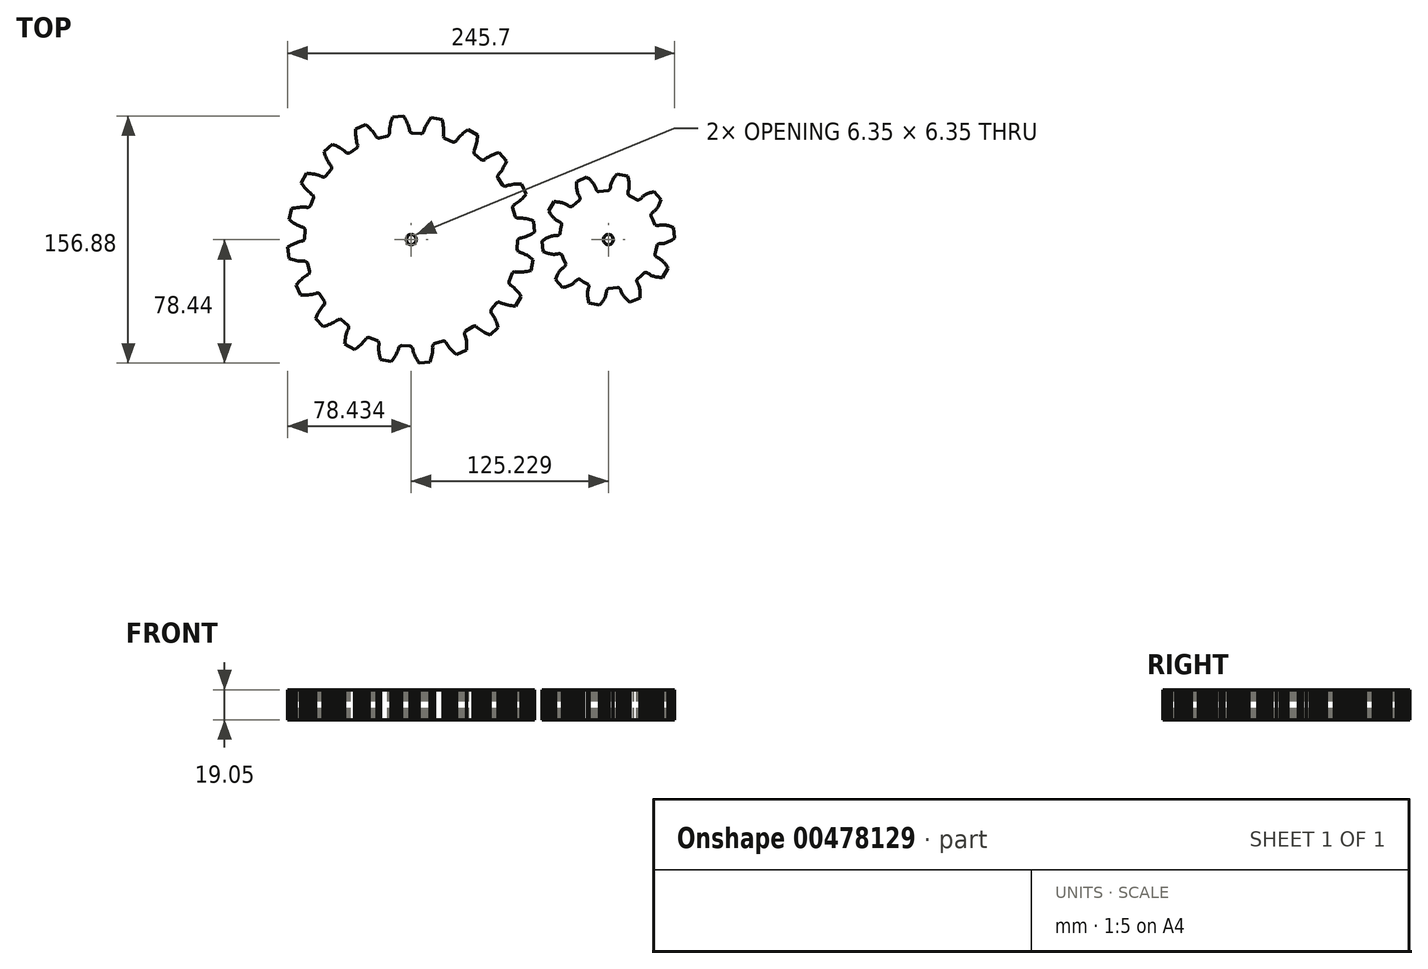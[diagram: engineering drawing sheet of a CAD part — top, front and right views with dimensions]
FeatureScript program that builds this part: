
annotation { "Feature Type Name" : "Feature", "Feature Type Description" : "" }
export const myFeature = defineFeature(function(context is Context, id is Id, definition is map)
    precondition{}
    {
        {
            var Q0;
            Q0=qCreatedBy(makeId("Top.planeOp"),FACE);
            var sketch = newSketch(context, id + "F0", { "sketchPlane" : qUnion([Q0])});
            skLineSegment(sketch, "E0", {"start": v(22.88, -6.1) * mm, "end": v(23.09, -6.86) * mm});
            skLineSegment(sketch, "E1", {"start": v(23.09, -6.86) * mm, "end": v(23.33, -7.16) * mm});
            skLineSegment(sketch, "E2", {"start": v(23.33, -7.16) * mm, "end": v(23.58, -7.39) * mm});
            skLineSegment(sketch, "E3", {"start": v(23.58, -7.39) * mm, "end": v(23.81, -7.8) * mm});
            skLineSegment(sketch, "E4", {"start": v(23.81, -7.8) * mm, "end": v(24.36, -7.91) * mm});
            skLineSegment(sketch, "E5", {"start": v(24.36, -7.91) * mm, "end": v(24.9, -8.06) * mm});
            skLineSegment(sketch, "E6", {"start": v(24.9, -8.06) * mm, "end": v(25.96, -8.43) * mm});
            skLineSegment(sketch, "E7", {"start": v(25.96, -8.43) * mm, "end": v(27.01, -8.88) * mm});
            skLineSegment(sketch, "E8", {"start": v(27.01, -8.88) * mm, "end": v(28.06, -9.39) * mm});
            skLineSegment(sketch, "E9", {"start": v(28.06, -9.39) * mm, "end": v(29.1, -9.95) * mm});
            skLineSegment(sketch, "E10", {"start": v(29.1, -9.95) * mm, "end": v(30.12, -10.57) * mm});
            skLineSegment(sketch, "E11", {"start": v(30.12, -10.57) * mm, "end": v(31.14, -11.24) * mm});
            skLineSegment(sketch, "E12", {"start": v(31.14, -11.24) * mm, "end": v(32.14, -11.96) * mm});
            skLineSegment(sketch, "E13", {"start": v(32.14, -11.96) * mm, "end": v(33.14, -12.72) * mm});
            skLineSegment(sketch, "E14", {"start": v(33.14, -12.72) * mm, "end": v(31.69, -19.6) * mm});
            skLineSegment(sketch, "E15", {"start": v(31.69, -19.6) * mm, "end": v(30.47, -19.9) * mm});
            skLineSegment(sketch, "E16", {"start": v(30.47, -19.9) * mm, "end": v(29.26, -20.15) * mm});
            skLineSegment(sketch, "E17", {"start": v(29.26, -20.15) * mm, "end": v(28.06, -20.35) * mm});
            skLineSegment(sketch, "E18", {"start": v(28.06, -20.35) * mm, "end": v(26.88, -20.5) * mm});
            skLineSegment(sketch, "E19", {"start": v(26.88, -20.5) * mm, "end": v(25.7, -20.6) * mm});
            skLineSegment(sketch, "E20", {"start": v(25.7, -20.6) * mm, "end": v(24.54, -20.65) * mm});
            skLineSegment(sketch, "E21", {"start": v(24.54, -20.65) * mm, "end": v(23.4, -20.64) * mm});
            skLineSegment(sketch, "E22", {"start": v(23.4, -20.64) * mm, "end": v(22.27, -20.55) * mm});
            skLineSegment(sketch, "E23", {"start": v(22.27, -20.55) * mm, "end": v(21.72, -20.47) * mm});
            skLineSegment(sketch, "E24", {"start": v(21.72, -20.47) * mm, "end": v(21.18, -20.35) * mm});
            skLineSegment(sketch, "E25", {"start": v(21.18, -20.35) * mm, "end": v(20.8, -20.64) * mm});
            skLineSegment(sketch, "E26", {"start": v(20.8, -20.64) * mm, "end": v(20.47, -20.74) * mm});
            skLineSegment(sketch, "E27", {"start": v(20.47, -20.74) * mm, "end": v(20.13, -20.92) * mm});
            skLineSegment(sketch, "E28", {"start": v(20.13, -20.92) * mm, "end": v(19.64, -21.53) * mm});
            skLineSegment(sketch, "E29", {"start": v(19.64, -21.53) * mm, "end": v(17.7, -26.6) * mm});
            skLineSegment(sketch, "E30", {"start": v(17.7, -26.6) * mm, "end": v(17.66, -27.38) * mm});
            skLineSegment(sketch, "E31", {"start": v(17.66, -27.38) * mm, "end": v(17.8, -27.74) * mm});
            skLineSegment(sketch, "E32", {"start": v(17.8, -27.74) * mm, "end": v(17.97, -28.04) * mm});
            skLineSegment(sketch, "E33", {"start": v(17.97, -28.04) * mm, "end": v(18.06, -28.5) * mm});
            skLineSegment(sketch, "E34", {"start": v(18.06, -28.5) * mm, "end": v(18.54, -28.78) * mm});
            skLineSegment(sketch, "E35", {"start": v(18.54, -28.78) * mm, "end": v(19, -29.09) * mm});
            skLineSegment(sketch, "E36", {"start": v(19, -29.09) * mm, "end": v(19.9, -29.77) * mm});
            skLineSegment(sketch, "E37", {"start": v(19.9, -29.77) * mm, "end": v(20.77, -30.52) * mm});
            skLineSegment(sketch, "E38", {"start": v(20.77, -30.52) * mm, "end": v(21.61, -31.32) * mm});
            skLineSegment(sketch, "E39", {"start": v(21.61, -31.32) * mm, "end": v(22.42, -32.18) * mm});
            skLineSegment(sketch, "E40", {"start": v(22.42, -32.18) * mm, "end": v(23.2, -33.09) * mm});
            skLineSegment(sketch, "E41", {"start": v(23.2, -33.09) * mm, "end": v(23.97, -34.04) * mm});
            skLineSegment(sketch, "E42", {"start": v(23.97, -34.04) * mm, "end": v(24.7, -35.03) * mm});
            skLineSegment(sketch, "E43", {"start": v(24.7, -35.03) * mm, "end": v(25.41, -36.06) * mm});
            skLineSegment(sketch, "E44", {"start": v(25.41, -36.06) * mm, "end": v(21.9, -42.16) * mm});
            skLineSegment(sketch, "E45", {"start": v(21.9, -42.16) * mm, "end": v(20.66, -42.07) * mm});
            skLineSegment(sketch, "E46", {"start": v(20.66, -42.07) * mm, "end": v(19.43, -41.93) * mm});
            skLineSegment(sketch, "E47", {"start": v(19.43, -41.93) * mm, "end": v(18.23, -41.76) * mm});
            skLineSegment(sketch, "E48", {"start": v(18.23, -41.76) * mm, "end": v(17.05, -41.53) * mm});
            skLineSegment(sketch, "E49", {"start": v(17.05, -41.53) * mm, "end": v(15.9, -41.27) * mm});
            skLineSegment(sketch, "E50", {"start": v(15.9, -41.27) * mm, "end": v(14.78, -40.95) * mm});
            skLineSegment(sketch, "E51", {"start": v(14.78, -40.95) * mm, "end": v(13.7, -40.58) * mm});
            skLineSegment(sketch, "E52", {"start": v(13.7, -40.58) * mm, "end": v(12.65, -40.15) * mm});
            skLineSegment(sketch, "E53", {"start": v(12.65, -40.15) * mm, "end": v(12.15, -39.9) * mm});
            skLineSegment(sketch, "E54", {"start": v(12.15, -39.9) * mm, "end": v(11.68, -39.62) * mm});
            skLineSegment(sketch, "E55", {"start": v(11.68, -39.62) * mm, "end": v(11.23, -39.78) * mm});
            skLineSegment(sketch, "E56", {"start": v(11.23, -39.78) * mm, "end": v(10.89, -39.78) * mm});
            skLineSegment(sketch, "E57", {"start": v(10.89, -39.78) * mm, "end": v(10.5, -39.84) * mm});
            skLineSegment(sketch, "E58", {"start": v(10.5, -39.84) * mm, "end": v(9.85, -40.27) * mm});
            skLineSegment(sketch, "E59", {"start": v(9.85, -40.27) * mm, "end": v(6.44, -44.5) * mm});
            skLineSegment(sketch, "E60", {"start": v(6.44, -44.5) * mm, "end": v(6.16, -45.22) * mm});
            skLineSegment(sketch, "E61", {"start": v(6.16, -45.22) * mm, "end": v(6.18, -45.61) * mm});
            skLineSegment(sketch, "E62", {"start": v(6.18, -45.61) * mm, "end": v(6.26, -45.94) * mm});
            skLineSegment(sketch, "E63", {"start": v(6.26, -45.94) * mm, "end": v(6.2, -46.42) * mm});
            skLineSegment(sketch, "E64", {"start": v(6.2, -46.42) * mm, "end": v(6.57, -46.83) * mm});
            skLineSegment(sketch, "E65", {"start": v(6.57, -46.83) * mm, "end": v(6.92, -47.26) * mm});
            skLineSegment(sketch, "E66", {"start": v(6.92, -47.26) * mm, "end": v(7.56, -48.19) * mm});
            skLineSegment(sketch, "E67", {"start": v(7.56, -48.19) * mm, "end": v(8.15, -49.17) * mm});
            skLineSegment(sketch, "E68", {"start": v(8.15, -49.17) * mm, "end": v(8.7, -50.2) * mm});
            skLineSegment(sketch, "E69", {"start": v(8.7, -50.2) * mm, "end": v(9.2, -51.26) * mm});
            skLineSegment(sketch, "E70", {"start": v(9.2, -51.26) * mm, "end": v(9.67, -52.37) * mm});
            skLineSegment(sketch, "E71", {"start": v(9.67, -52.37) * mm, "end": v(10.1, -53.5) * mm});
            skLineSegment(sketch, "E72", {"start": v(10.1, -53.5) * mm, "end": v(10.5, -54.68) * mm});
            skLineSegment(sketch, "E73", {"start": v(10.5, -54.68) * mm, "end": v(10.85, -55.87) * mm});
            skLineSegment(sketch, "E74", {"start": v(10.85, -55.87) * mm, "end": v(5.63, -60.6) * mm});
            skLineSegment(sketch, "E75", {"start": v(5.63, -60.6) * mm, "end": v(4.47, -60.12) * mm});
            skLineSegment(sketch, "E76", {"start": v(4.47, -60.12) * mm, "end": v(3.35, -59.61) * mm});
            skLineSegment(sketch, "E77", {"start": v(3.35, -59.61) * mm, "end": v(2.26, -59.07) * mm});
            skLineSegment(sketch, "E78", {"start": v(2.26, -59.07) * mm, "end": v(1.2, -58.5) * mm});
            skLineSegment(sketch, "E79", {"start": v(1.2, -58.5) * mm, "end": v(0.2, -57.89) * mm});
            skLineSegment(sketch, "E80", {"start": v(0.2, -57.89) * mm, "end": v(-0.77, -57.24) * mm});
            skLineSegment(sketch, "E81", {"start": v(-0.77, -57.24) * mm, "end": v(-1.69, -56.55) * mm});
            skLineSegment(sketch, "E82", {"start": v(-1.69, -56.55) * mm, "end": v(-2.54, -55.82) * mm});
            skLineSegment(sketch, "E83", {"start": v(-2.54, -55.82) * mm, "end": v(-2.94, -55.43) * mm});
            skLineSegment(sketch, "E84", {"start": v(-2.94, -55.43) * mm, "end": v(-3.31, -55.01) * mm});
            skLineSegment(sketch, "E85", {"start": v(-3.31, -55.01) * mm, "end": v(-3.79, -55.03) * mm});
            skLineSegment(sketch, "E86", {"start": v(-3.79, -55.03) * mm, "end": v(-4.11, -54.92) * mm});
            skLineSegment(sketch, "E87", {"start": v(-4.11, -54.92) * mm, "end": v(-4.5, -54.86) * mm});
            skLineSegment(sketch, "E88", {"start": v(-4.5, -54.86) * mm, "end": v(-5.25, -55.06) * mm});
            skLineSegment(sketch, "E89", {"start": v(-5.25, -55.06) * mm, "end": v(-9.8, -58.03) * mm});
            skLineSegment(sketch, "E90", {"start": v(-9.8, -58.03) * mm, "end": v(-10.29, -58.64) * mm});
            skLineSegment(sketch, "E91", {"start": v(-10.29, -58.64) * mm, "end": v(-10.39, -59.02) * mm});
            skLineSegment(sketch, "E92", {"start": v(-10.39, -59.02) * mm, "end": v(-10.42, -59.35) * mm});
            skLineSegment(sketch, "E93", {"start": v(-10.42, -59.35) * mm, "end": v(-10.63, -59.79) * mm});
            skLineSegment(sketch, "E94", {"start": v(-10.63, -59.79) * mm, "end": v(-10.4, -60.29) * mm});
            skLineSegment(sketch, "E95", {"start": v(-10.4, -60.29) * mm, "end": v(-10.2, -60.81) * mm});
            skLineSegment(sketch, "E96", {"start": v(-10.2, -60.81) * mm, "end": v(-9.87, -61.9) * mm});
            skLineSegment(sketch, "E97", {"start": v(-9.87, -61.9) * mm, "end": v(-9.61, -63) * mm});
            skLineSegment(sketch, "E98", {"start": v(-9.61, -63) * mm, "end": v(-9.4, -64.15) * mm});
            skLineSegment(sketch, "E99", {"start": v(-9.4, -64.15) * mm, "end": v(-9.26, -65.32) * mm});
            skLineSegment(sketch, "E100", {"start": v(-9.26, -65.32) * mm, "end": v(-9.16, -66.52) * mm});
            skLineSegment(sketch, "E101", {"start": v(-9.16, -66.52) * mm, "end": v(-9.1, -67.73) * mm});
            skLineSegment(sketch, "E102", {"start": v(-9.1, -67.73) * mm, "end": v(-9.09, -68.97) * mm});
            skLineSegment(sketch, "E103", {"start": v(-9.09, -68.97) * mm, "end": v(-9.12, -70.22) * mm});
            skLineSegment(sketch, "E104", {"start": v(-9.12, -70.22) * mm, "end": v(-15.54, -73.1) * mm});
            skLineSegment(sketch, "E105", {"start": v(-15.54, -73.1) * mm, "end": v(-16.5, -72.28) * mm});
            skLineSegment(sketch, "E106", {"start": v(-16.5, -72.28) * mm, "end": v(-17.41, -71.45) * mm});
            skLineSegment(sketch, "E107", {"start": v(-17.41, -71.45) * mm, "end": v(-18.28, -70.6) * mm});
            skLineSegment(sketch, "E108", {"start": v(-18.28, -70.6) * mm, "end": v(-19.1, -69.73) * mm});
            skLineSegment(sketch, "E109", {"start": v(-19.1, -69.73) * mm, "end": v(-19.88, -68.84) * mm});
            skLineSegment(sketch, "E110", {"start": v(-19.88, -68.84) * mm, "end": v(-20.6, -67.92) * mm});
            skLineSegment(sketch, "E111", {"start": v(-20.6, -67.92) * mm, "end": v(-21.26, -66.99) * mm});
            skLineSegment(sketch, "E112", {"start": v(-21.26, -66.99) * mm, "end": v(-21.84, -66.02) * mm});
            skLineSegment(sketch, "E113", {"start": v(-21.84, -66.02) * mm, "end": v(-22.1, -65.53) * mm});
            skLineSegment(sketch, "E114", {"start": v(-22.1, -65.53) * mm, "end": v(-22.32, -65.02) * mm});
            skLineSegment(sketch, "E115", {"start": v(-22.32, -65.02) * mm, "end": v(-22.78, -64.89) * mm});
            skLineSegment(sketch, "E116", {"start": v(-22.78, -64.89) * mm, "end": v(-23.06, -64.69) * mm});
            skLineSegment(sketch, "E117", {"start": v(-23.06, -64.69) * mm, "end": v(-23.4, -64.51) * mm});
            skLineSegment(sketch, "E118", {"start": v(-23.4, -64.51) * mm, "end": v(-24.18, -64.47) * mm});
            skLineSegment(sketch, "E119", {"start": v(-24.18, -64.47) * mm, "end": v(-29.43, -65.9) * mm});
            skLineSegment(sketch, "E120", {"start": v(-29.43, -65.9) * mm, "end": v(-30.08, -66.32) * mm});
            skLineSegment(sketch, "E121", {"start": v(-30.08, -66.32) * mm, "end": v(-30.3, -66.64) * mm});
            skLineSegment(sketch, "E122", {"start": v(-30.3, -66.64) * mm, "end": v(-30.43, -66.95) * mm});
            skLineSegment(sketch, "E123", {"start": v(-30.43, -66.95) * mm, "end": v(-30.75, -67.3) * mm});
            skLineSegment(sketch, "E124", {"start": v(-30.75, -67.3) * mm, "end": v(-30.7, -67.85) * mm});
            skLineSegment(sketch, "E125", {"start": v(-30.7, -67.85) * mm, "end": v(-30.67, -68.4) * mm});
            skLineSegment(sketch, "E126", {"start": v(-30.67, -68.4) * mm, "end": v(-30.69, -69.54) * mm});
            skLineSegment(sketch, "E127", {"start": v(-30.69, -69.54) * mm, "end": v(-30.79, -70.68) * mm});
            skLineSegment(sketch, "E128", {"start": v(-30.79, -70.68) * mm, "end": v(-30.95, -71.83) * mm});
            skLineSegment(sketch, "E129", {"start": v(-30.95, -71.83) * mm, "end": v(-31.17, -72.99) * mm});
            skLineSegment(sketch, "E130", {"start": v(-31.17, -72.99) * mm, "end": v(-31.44, -74.16) * mm});
            skLineSegment(sketch, "E131", {"start": v(-31.44, -74.16) * mm, "end": v(-31.76, -75.33) * mm});
            skLineSegment(sketch, "E132", {"start": v(-31.76, -75.33) * mm, "end": v(-32.13, -76.5) * mm});
            skLineSegment(sketch, "E133", {"start": v(-32.13, -76.5) * mm, "end": v(-32.55, -77.69) * mm});
            skLineSegment(sketch, "E134", {"start": v(-32.55, -77.69) * mm, "end": v(-39.54, -78.44) * mm});
            skLineSegment(sketch, "E135", {"start": v(-39.54, -78.44) * mm, "end": v(-40.2, -77.37) * mm});
            skLineSegment(sketch, "E136", {"start": v(-40.2, -77.37) * mm, "end": v(-40.81, -76.3) * mm});
            skLineSegment(sketch, "E137", {"start": v(-40.81, -76.3) * mm, "end": v(-41.38, -75.22) * mm});
            skLineSegment(sketch, "E138", {"start": v(-41.38, -75.22) * mm, "end": v(-41.89, -74.14) * mm});
            skLineSegment(sketch, "E139", {"start": v(-41.89, -74.14) * mm, "end": v(-42.35, -73.05) * mm});
            skLineSegment(sketch, "E140", {"start": v(-42.35, -73.05) * mm, "end": v(-42.75, -71.96) * mm});
            skLineSegment(sketch, "E141", {"start": v(-42.75, -71.96) * mm, "end": v(-43.09, -70.87) * mm});
            skLineSegment(sketch, "E142", {"start": v(-43.09, -70.87) * mm, "end": v(-43.35, -69.77) * mm});
            skLineSegment(sketch, "E143", {"start": v(-43.35, -69.77) * mm, "end": v(-43.44, -69.22) * mm});
            skLineSegment(sketch, "E144", {"start": v(-43.44, -69.22) * mm, "end": v(-43.5, -68.67) * mm});
            skLineSegment(sketch, "E145", {"start": v(-43.5, -68.67) * mm, "end": v(-43.9, -68.4) * mm});
            skLineSegment(sketch, "E146", {"start": v(-43.9, -68.4) * mm, "end": v(-44.1, -68.12) * mm});
            skLineSegment(sketch, "E147", {"start": v(-44.1, -68.12) * mm, "end": v(-44.37, -67.85) * mm});
            skLineSegment(sketch, "E148", {"start": v(-44.37, -67.85) * mm, "end": v(-45.1, -67.57) * mm});
            skLineSegment(sketch, "E149", {"start": v(-45.1, -67.57) * mm, "end": v(-50.52, -67.3) * mm});
            skLineSegment(sketch, "E150", {"start": v(-50.52, -67.3) * mm, "end": v(-51.27, -67.5) * mm});
            skLineSegment(sketch, "E151", {"start": v(-51.27, -67.5) * mm, "end": v(-51.58, -67.75) * mm});
            skLineSegment(sketch, "E152", {"start": v(-51.58, -67.75) * mm, "end": v(-51.8, -68) * mm});
            skLineSegment(sketch, "E153", {"start": v(-51.8, -68) * mm, "end": v(-52.22, -68.23) * mm});
            skLineSegment(sketch, "E154", {"start": v(-52.22, -68.23) * mm, "end": v(-52.33, -68.77) * mm});
            skLineSegment(sketch, "E155", {"start": v(-52.33, -68.77) * mm, "end": v(-52.48, -69.3) * mm});
            skLineSegment(sketch, "E156", {"start": v(-52.48, -69.3) * mm, "end": v(-52.85, -70.37) * mm});
            skLineSegment(sketch, "E157", {"start": v(-52.85, -70.37) * mm, "end": v(-53.3, -71.43) * mm});
            skLineSegment(sketch, "E158", {"start": v(-53.3, -71.43) * mm, "end": v(-53.8, -72.48) * mm});
            skLineSegment(sketch, "E159", {"start": v(-53.8, -72.48) * mm, "end": v(-54.37, -73.51) * mm});
            skLineSegment(sketch, "E160", {"start": v(-54.37, -73.51) * mm, "end": v(-54.99, -74.54) * mm});
            skLineSegment(sketch, "E161", {"start": v(-54.99, -74.54) * mm, "end": v(-55.66, -75.55) * mm});
            skLineSegment(sketch, "E162", {"start": v(-55.66, -75.55) * mm, "end": v(-56.37, -76.56) * mm});
            skLineSegment(sketch, "E163", {"start": v(-56.37, -76.56) * mm, "end": v(-57.14, -77.55) * mm});
            skLineSegment(sketch, "E164", {"start": v(-57.14, -77.55) * mm, "end": v(-64.02, -76.1) * mm});
            skLineSegment(sketch, "E165", {"start": v(-64.02, -76.1) * mm, "end": v(-64.32, -74.89) * mm});
            skLineSegment(sketch, "E166", {"start": v(-64.32, -74.89) * mm, "end": v(-64.57, -73.68) * mm});
            skLineSegment(sketch, "E167", {"start": v(-64.57, -73.68) * mm, "end": v(-64.77, -72.48) * mm});
            skLineSegment(sketch, "E168", {"start": v(-64.77, -72.48) * mm, "end": v(-64.92, -71.3) * mm});
            skLineSegment(sketch, "E169", {"start": v(-64.92, -71.3) * mm, "end": v(-65.03, -70.11) * mm});
            skLineSegment(sketch, "E170", {"start": v(-65.03, -70.11) * mm, "end": v(-65.07, -68.95) * mm});
            skLineSegment(sketch, "E171", {"start": v(-65.07, -68.95) * mm, "end": v(-65.05, -67.8) * mm});
            skLineSegment(sketch, "E172", {"start": v(-65.05, -67.8) * mm, "end": v(-64.96, -66.68) * mm});
            skLineSegment(sketch, "E173", {"start": v(-64.96, -66.68) * mm, "end": v(-64.88, -66.13) * mm});
            skLineSegment(sketch, "E174", {"start": v(-64.88, -66.13) * mm, "end": v(-64.76, -65.6) * mm});
            skLineSegment(sketch, "E175", {"start": v(-64.76, -65.6) * mm, "end": v(-65.05, -65.21) * mm});
            skLineSegment(sketch, "E176", {"start": v(-65.05, -65.21) * mm, "end": v(-65.16, -64.89) * mm});
            skLineSegment(sketch, "E177", {"start": v(-65.16, -64.89) * mm, "end": v(-65.34, -64.54) * mm});
            skLineSegment(sketch, "E178", {"start": v(-65.34, -64.54) * mm, "end": v(-65.94, -64.05) * mm});
            skLineSegment(sketch, "E179", {"start": v(-65.94, -64.05) * mm, "end": v(-71.02, -62.12) * mm});
            skLineSegment(sketch, "E180", {"start": v(-71.02, -62.12) * mm, "end": v(-71.8, -62.08) * mm});
            skLineSegment(sketch, "E181", {"start": v(-71.8, -62.08) * mm, "end": v(-72.16, -62.22) * mm});
            skLineSegment(sketch, "E182", {"start": v(-72.16, -62.22) * mm, "end": v(-72.45, -62.39) * mm});
            skLineSegment(sketch, "E183", {"start": v(-72.45, -62.39) * mm, "end": v(-72.92, -62.48) * mm});
            skLineSegment(sketch, "E184", {"start": v(-72.92, -62.48) * mm, "end": v(-73.2, -62.96) * mm});
            skLineSegment(sketch, "E185", {"start": v(-73.2, -62.96) * mm, "end": v(-73.5, -63.43) * mm});
            skLineSegment(sketch, "E186", {"start": v(-73.5, -63.43) * mm, "end": v(-74.18, -64.32) * mm});
            skLineSegment(sketch, "E187", {"start": v(-74.18, -64.32) * mm, "end": v(-74.93, -65.2) * mm});
            skLineSegment(sketch, "E188", {"start": v(-74.93, -65.2) * mm, "end": v(-75.74, -66.03) * mm});
            skLineSegment(sketch, "E189", {"start": v(-75.74, -66.03) * mm, "end": v(-76.6, -66.84) * mm});
            skLineSegment(sketch, "E190", {"start": v(-76.6, -66.84) * mm, "end": v(-77.5, -67.62) * mm});
            skLineSegment(sketch, "E191", {"start": v(-77.5, -67.62) * mm, "end": v(-78.46, -68.38) * mm});
            skLineSegment(sketch, "E192", {"start": v(-78.46, -68.38) * mm, "end": v(-79.45, -69.12) * mm});
            skLineSegment(sketch, "E193", {"start": v(-79.45, -69.12) * mm, "end": v(-80.48, -69.83) * mm});
            skLineSegment(sketch, "E194", {"start": v(-80.48, -69.83) * mm, "end": v(-86.58, -66.32) * mm});
            skLineSegment(sketch, "E195", {"start": v(-86.58, -66.32) * mm, "end": v(-86.48, -65.07) * mm});
            skLineSegment(sketch, "E196", {"start": v(-86.48, -65.07) * mm, "end": v(-86.35, -63.85) * mm});
            skLineSegment(sketch, "E197", {"start": v(-86.35, -63.85) * mm, "end": v(-86.17, -62.64) * mm});
            skLineSegment(sketch, "E198", {"start": v(-86.17, -62.64) * mm, "end": v(-85.95, -61.47) * mm});
            skLineSegment(sketch, "E199", {"start": v(-85.95, -61.47) * mm, "end": v(-85.68, -60.31) * mm});
            skLineSegment(sketch, "E200", {"start": v(-85.68, -60.31) * mm, "end": v(-85.37, -59.2) * mm});
            skLineSegment(sketch, "E201", {"start": v(-85.37, -59.2) * mm, "end": v(-85, -58.11) * mm});
            skLineSegment(sketch, "E202", {"start": v(-85, -58.11) * mm, "end": v(-84.56, -57.07) * mm});
            skLineSegment(sketch, "E203", {"start": v(-84.56, -57.07) * mm, "end": v(-84.31, -56.57) * mm});
            skLineSegment(sketch, "E204", {"start": v(-84.31, -56.57) * mm, "end": v(-84.04, -56.1) * mm});
            skLineSegment(sketch, "E205", {"start": v(-84.04, -56.1) * mm, "end": v(-84.2, -55.64) * mm});
            skLineSegment(sketch, "E206", {"start": v(-84.2, -55.64) * mm, "end": v(-84.2, -55.3) * mm});
            skLineSegment(sketch, "E207", {"start": v(-84.2, -55.3) * mm, "end": v(-84.26, -54.92) * mm});
            skLineSegment(sketch, "E208", {"start": v(-84.26, -54.92) * mm, "end": v(-84.68, -54.27) * mm});
            skLineSegment(sketch, "E209", {"start": v(-84.68, -54.27) * mm, "end": v(-88.91, -50.86) * mm});
            skLineSegment(sketch, "E210", {"start": v(-88.91, -50.86) * mm, "end": v(-89.64, -50.58) * mm});
            skLineSegment(sketch, "E211", {"start": v(-89.64, -50.58) * mm, "end": v(-90.03, -50.6) * mm});
            skLineSegment(sketch, "E212", {"start": v(-90.03, -50.6) * mm, "end": v(-90.36, -50.67) * mm});
            skLineSegment(sketch, "E213", {"start": v(-90.36, -50.67) * mm, "end": v(-90.83, -50.61) * mm});
            skLineSegment(sketch, "E214", {"start": v(-90.83, -50.61) * mm, "end": v(-91.24, -50.99) * mm});
            skLineSegment(sketch, "E215", {"start": v(-91.24, -50.99) * mm, "end": v(-91.68, -51.33) * mm});
            skLineSegment(sketch, "E216", {"start": v(-91.68, -51.33) * mm, "end": v(-92.6, -51.98) * mm});
            skLineSegment(sketch, "E217", {"start": v(-92.6, -51.98) * mm, "end": v(-93.58, -52.57) * mm});
            skLineSegment(sketch, "E218", {"start": v(-93.58, -52.57) * mm, "end": v(-94.61, -53.12) * mm});
            skLineSegment(sketch, "E219", {"start": v(-94.61, -53.12) * mm, "end": v(-95.68, -53.62) * mm});
            skLineSegment(sketch, "E220", {"start": v(-95.68, -53.62) * mm, "end": v(-96.78, -54.09) * mm});
            skLineSegment(sketch, "E221", {"start": v(-96.78, -54.09) * mm, "end": v(-97.92, -54.52) * mm});
            skLineSegment(sketch, "E222", {"start": v(-97.92, -54.52) * mm, "end": v(-99.1, -54.9) * mm});
            skLineSegment(sketch, "E223", {"start": v(-99.1, -54.9) * mm, "end": v(-100.3, -55.27) * mm});
            skLineSegment(sketch, "E224", {"start": v(-100.3, -55.27) * mm, "end": v(-105, -50.05) * mm});
            skLineSegment(sketch, "E225", {"start": v(-105, -50.05) * mm, "end": v(-104.53, -48.89) * mm});
            skLineSegment(sketch, "E226", {"start": v(-104.53, -48.89) * mm, "end": v(-104.03, -47.76) * mm});
            skLineSegment(sketch, "E227", {"start": v(-104.03, -47.76) * mm, "end": v(-103.49, -46.67) * mm});
            skLineSegment(sketch, "E228", {"start": v(-103.49, -46.67) * mm, "end": v(-102.91, -45.62) * mm});
            skLineSegment(sketch, "E229", {"start": v(-102.91, -45.62) * mm, "end": v(-102.3, -44.61) * mm});
            skLineSegment(sketch, "E230", {"start": v(-102.3, -44.61) * mm, "end": v(-101.65, -43.64) * mm});
            skLineSegment(sketch, "E231", {"start": v(-101.65, -43.64) * mm, "end": v(-100.97, -42.73) * mm});
            skLineSegment(sketch, "E232", {"start": v(-100.97, -42.73) * mm, "end": v(-100.23, -41.87) * mm});
            skLineSegment(sketch, "E233", {"start": v(-100.23, -41.87) * mm, "end": v(-99.84, -41.47) * mm});
            skLineSegment(sketch, "E234", {"start": v(-99.84, -41.47) * mm, "end": v(-99.43, -41.1) * mm});
            skLineSegment(sketch, "E235", {"start": v(-99.43, -41.1) * mm, "end": v(-99.44, -40.63) * mm});
            skLineSegment(sketch, "E236", {"start": v(-99.44, -40.63) * mm, "end": v(-99.34, -40.3) * mm});
            skLineSegment(sketch, "E237", {"start": v(-99.34, -40.3) * mm, "end": v(-99.28, -39.92) * mm});
            skLineSegment(sketch, "E238", {"start": v(-99.28, -39.92) * mm, "end": v(-99.48, -39.17) * mm});
            skLineSegment(sketch, "E239", {"start": v(-99.48, -39.17) * mm, "end": v(-102.45, -34.62) * mm});
            skLineSegment(sketch, "E240", {"start": v(-102.45, -34.62) * mm, "end": v(-103.06, -34.13) * mm});
            skLineSegment(sketch, "E241", {"start": v(-103.06, -34.13) * mm, "end": v(-103.43, -34.03) * mm});
            skLineSegment(sketch, "E242", {"start": v(-103.43, -34.03) * mm, "end": v(-103.77, -34) * mm});
            skLineSegment(sketch, "E243", {"start": v(-103.77, -34) * mm, "end": v(-104.2, -33.79) * mm});
            skLineSegment(sketch, "E244", {"start": v(-104.2, -33.79) * mm, "end": v(-104.7, -34.02) * mm});
            skLineSegment(sketch, "E245", {"start": v(-104.7, -34.02) * mm, "end": v(-105.23, -34.22) * mm});
            skLineSegment(sketch, "E246", {"start": v(-105.23, -34.22) * mm, "end": v(-106.3, -34.54) * mm});
            skLineSegment(sketch, "E247", {"start": v(-106.3, -34.54) * mm, "end": v(-107.42, -34.8) * mm});
            skLineSegment(sketch, "E248", {"start": v(-107.42, -34.8) * mm, "end": v(-108.57, -35) * mm});
            skLineSegment(sketch, "E249", {"start": v(-108.57, -35) * mm, "end": v(-109.74, -35.16) * mm});
            skLineSegment(sketch, "E250", {"start": v(-109.74, -35.16) * mm, "end": v(-110.93, -35.26) * mm});
            skLineSegment(sketch, "E251", {"start": v(-110.93, -35.26) * mm, "end": v(-112.15, -35.31) * mm});
            skLineSegment(sketch, "E252", {"start": v(-112.15, -35.31) * mm, "end": v(-113.38, -35.33) * mm});
            skLineSegment(sketch, "E253", {"start": v(-113.38, -35.33) * mm, "end": v(-114.63, -35.3) * mm});
            skLineSegment(sketch, "E254", {"start": v(-114.63, -35.3) * mm, "end": v(-117.5, -28.87) * mm});
            skLineSegment(sketch, "E255", {"start": v(-117.5, -28.87) * mm, "end": v(-116.7, -27.92) * mm});
            skLineSegment(sketch, "E256", {"start": v(-116.7, -27.92) * mm, "end": v(-115.87, -27) * mm});
            skLineSegment(sketch, "E257", {"start": v(-115.87, -27) * mm, "end": v(-115.02, -26.14) * mm});
            skLineSegment(sketch, "E258", {"start": v(-115.02, -26.14) * mm, "end": v(-114.15, -25.31) * mm});
            skLineSegment(sketch, "E259", {"start": v(-114.15, -25.31) * mm, "end": v(-113.25, -24.54) * mm});
            skLineSegment(sketch, "E260", {"start": v(-113.25, -24.54) * mm, "end": v(-112.34, -23.82) * mm});
            skLineSegment(sketch, "E261", {"start": v(-112.34, -23.82) * mm, "end": v(-111.4, -23.16) * mm});
            skLineSegment(sketch, "E262", {"start": v(-111.4, -23.16) * mm, "end": v(-110.44, -22.57) * mm});
            skLineSegment(sketch, "E263", {"start": v(-110.44, -22.57) * mm, "end": v(-109.95, -22.31) * mm});
            skLineSegment(sketch, "E264", {"start": v(-109.95, -22.31) * mm, "end": v(-109.44, -22.1) * mm});
            skLineSegment(sketch, "E265", {"start": v(-109.44, -22.1) * mm, "end": v(-109.3, -21.63) * mm});
            skLineSegment(sketch, "E266", {"start": v(-109.3, -21.63) * mm, "end": v(-109.1, -21.36) * mm});
            skLineSegment(sketch, "E267", {"start": v(-109.1, -21.36) * mm, "end": v(-108.93, -21.01) * mm});
            skLineSegment(sketch, "E268", {"start": v(-108.93, -21.01) * mm, "end": v(-108.89, -20.23) * mm});
            skLineSegment(sketch, "E269", {"start": v(-108.89, -20.23) * mm, "end": v(-110.3, -14.99) * mm});
            skLineSegment(sketch, "E270", {"start": v(-110.3, -14.99) * mm, "end": v(-110.73, -14.34) * mm});
            skLineSegment(sketch, "E271", {"start": v(-110.73, -14.34) * mm, "end": v(-111.06, -14.13) * mm});
            skLineSegment(sketch, "E272", {"start": v(-111.06, -14.13) * mm, "end": v(-111.37, -13.99) * mm});
            skLineSegment(sketch, "E273", {"start": v(-111.37, -13.99) * mm, "end": v(-111.72, -13.66) * mm});
            skLineSegment(sketch, "E274", {"start": v(-111.72, -13.66) * mm, "end": v(-112.27, -13.72) * mm});
            skLineSegment(sketch, "E275", {"start": v(-112.27, -13.72) * mm, "end": v(-112.82, -13.75) * mm});
            skLineSegment(sketch, "E276", {"start": v(-112.82, -13.75) * mm, "end": v(-113.95, -13.73) * mm});
            skLineSegment(sketch, "E277", {"start": v(-113.95, -13.73) * mm, "end": v(-115.1, -13.63) * mm});
            skLineSegment(sketch, "E278", {"start": v(-115.1, -13.63) * mm, "end": v(-116.25, -13.47) * mm});
            skLineSegment(sketch, "E279", {"start": v(-116.25, -13.47) * mm, "end": v(-117.4, -13.25) * mm});
            skLineSegment(sketch, "E280", {"start": v(-117.4, -13.25) * mm, "end": v(-118.57, -12.98) * mm});
            skLineSegment(sketch, "E281", {"start": v(-118.57, -12.98) * mm, "end": v(-119.75, -12.66) * mm});
            skLineSegment(sketch, "E282", {"start": v(-119.75, -12.66) * mm, "end": v(-120.92, -12.28) * mm});
            skLineSegment(sketch, "E283", {"start": v(-120.92, -12.28) * mm, "end": v(-122.1, -11.87) * mm});
            skLineSegment(sketch, "E284", {"start": v(-122.1, -11.87) * mm, "end": v(-122.85, -4.87) * mm});
            skLineSegment(sketch, "E285", {"start": v(-122.85, -4.87) * mm, "end": v(-121.79, -4.21) * mm});
            skLineSegment(sketch, "E286", {"start": v(-121.79, -4.21) * mm, "end": v(-120.72, -3.6) * mm});
            skLineSegment(sketch, "E287", {"start": v(-120.72, -3.6) * mm, "end": v(-119.64, -3.04) * mm});
            skLineSegment(sketch, "E288", {"start": v(-119.64, -3.04) * mm, "end": v(-118.56, -2.53) * mm});
            skLineSegment(sketch, "E289", {"start": v(-118.56, -2.53) * mm, "end": v(-117.47, -2.07) * mm});
            skLineSegment(sketch, "E290", {"start": v(-117.47, -2.07) * mm, "end": v(-116.38, -1.66) * mm});
            skLineSegment(sketch, "E291", {"start": v(-116.38, -1.66) * mm, "end": v(-115.28, -1.33) * mm});
            skLineSegment(sketch, "E292", {"start": v(-115.28, -1.33) * mm, "end": v(-114.18, -1.07) * mm});
            skLineSegment(sketch, "E293", {"start": v(-114.18, -1.07) * mm, "end": v(-113.63, -0.97) * mm});
            skLineSegment(sketch, "E294", {"start": v(-113.63, -0.97) * mm, "end": v(-113.08, -0.92) * mm});
            skLineSegment(sketch, "E295", {"start": v(-113.08, -0.92) * mm, "end": v(-112.81, -0.52) * mm});
            skLineSegment(sketch, "E296", {"start": v(-112.81, -0.52) * mm, "end": v(-112.54, -0.32) * mm});
            skLineSegment(sketch, "E297", {"start": v(-112.54, -0.32) * mm, "end": v(-112.26, -0.05) * mm});
            skLineSegment(sketch, "E298", {"start": v(-112.26, -0.05) * mm, "end": v(-111.99, 0.68) * mm});
            skLineSegment(sketch, "E299", {"start": v(-111.99, 0.68) * mm, "end": v(-111.71, 6.1) * mm});
            skLineSegment(sketch, "E300", {"start": v(-111.71, 6.1) * mm, "end": v(-111.92, 6.86) * mm});
            skLineSegment(sketch, "E301", {"start": v(-111.92, 6.86) * mm, "end": v(-112.16, 7.16) * mm});
            skLineSegment(sketch, "E302", {"start": v(-112.16, 7.16) * mm, "end": v(-112.42, 7.38) * mm});
            skLineSegment(sketch, "E303", {"start": v(-112.42, 7.38) * mm, "end": v(-112.65, 7.8) * mm});
            skLineSegment(sketch, "E304", {"start": v(-112.65, 7.8) * mm, "end": v(-113.19, 7.91) * mm});
            skLineSegment(sketch, "E305", {"start": v(-113.19, 7.91) * mm, "end": v(-113.72, 8.06) * mm});
            skLineSegment(sketch, "E306", {"start": v(-113.72, 8.06) * mm, "end": v(-114.8, 8.43) * mm});
            skLineSegment(sketch, "E307", {"start": v(-114.8, 8.43) * mm, "end": v(-115.85, 8.88) * mm});
            skLineSegment(sketch, "E308", {"start": v(-115.85, 8.88) * mm, "end": v(-116.9, 9.39) * mm});
            skLineSegment(sketch, "E309", {"start": v(-116.9, 9.39) * mm, "end": v(-117.93, 9.95) * mm});
            skLineSegment(sketch, "E310", {"start": v(-117.93, 9.95) * mm, "end": v(-118.95, 10.57) * mm});
            skLineSegment(sketch, "E311", {"start": v(-118.95, 10.57) * mm, "end": v(-119.97, 11.24) * mm});
            skLineSegment(sketch, "E312", {"start": v(-119.97, 11.24) * mm, "end": v(-120.97, 11.96) * mm});
            skLineSegment(sketch, "E313", {"start": v(-120.97, 11.96) * mm, "end": v(-121.97, 12.72) * mm});
            skLineSegment(sketch, "E314", {"start": v(-121.97, 12.72) * mm, "end": v(-120.52, 19.6) * mm});
            skLineSegment(sketch, "E315", {"start": v(-120.52, 19.6) * mm, "end": v(-119.3, 19.9) * mm});
            skLineSegment(sketch, "E316", {"start": v(-119.3, 19.9) * mm, "end": v(-118.1, 20.15) * mm});
            skLineSegment(sketch, "E317", {"start": v(-118.1, 20.15) * mm, "end": v(-116.9, 20.35) * mm});
            skLineSegment(sketch, "E318", {"start": v(-116.9, 20.35) * mm, "end": v(-115.7, 20.5) * mm});
            skLineSegment(sketch, "E319", {"start": v(-115.7, 20.5) * mm, "end": v(-114.53, 20.6) * mm});
            skLineSegment(sketch, "E320", {"start": v(-114.53, 20.6) * mm, "end": v(-113.37, 20.65) * mm});
            skLineSegment(sketch, "E321", {"start": v(-113.37, 20.65) * mm, "end": v(-112.22, 20.64) * mm});
            skLineSegment(sketch, "E322", {"start": v(-112.22, 20.64) * mm, "end": v(-111.1, 20.55) * mm});
            skLineSegment(sketch, "E323", {"start": v(-111.1, 20.55) * mm, "end": v(-110.55, 20.47) * mm});
            skLineSegment(sketch, "E324", {"start": v(-110.55, 20.47) * mm, "end": v(-110, 20.35) * mm});
            skLineSegment(sketch, "E325", {"start": v(-110, 20.35) * mm, "end": v(-109.63, 20.64) * mm});
            skLineSegment(sketch, "E326", {"start": v(-109.63, 20.64) * mm, "end": v(-109.3, 20.74) * mm});
            skLineSegment(sketch, "E327", {"start": v(-109.3, 20.74) * mm, "end": v(-108.96, 20.92) * mm});
            skLineSegment(sketch, "E328", {"start": v(-108.96, 20.92) * mm, "end": v(-108.47, 21.53) * mm});
            skLineSegment(sketch, "E329", {"start": v(-108.47, 21.53) * mm, "end": v(-106.53, 26.6) * mm});
            skLineSegment(sketch, "E330", {"start": v(-106.53, 26.6) * mm, "end": v(-106.5, 27.38) * mm});
            skLineSegment(sketch, "E331", {"start": v(-106.5, 27.38) * mm, "end": v(-106.63, 27.74) * mm});
            skLineSegment(sketch, "E332", {"start": v(-106.63, 27.74) * mm, "end": v(-106.8, 28.04) * mm});
            skLineSegment(sketch, "E333", {"start": v(-106.8, 28.04) * mm, "end": v(-106.9, 28.5) * mm});
            skLineSegment(sketch, "E334", {"start": v(-106.9, 28.5) * mm, "end": v(-107.38, 28.78) * mm});
            skLineSegment(sketch, "E335", {"start": v(-107.38, 28.78) * mm, "end": v(-107.84, 29.09) * mm});
            skLineSegment(sketch, "E336", {"start": v(-107.84, 29.09) * mm, "end": v(-108.74, 29.77) * mm});
            skLineSegment(sketch, "E337", {"start": v(-108.74, 29.77) * mm, "end": v(-109.6, 30.52) * mm});
            skLineSegment(sketch, "E338", {"start": v(-109.6, 30.52) * mm, "end": v(-110.44, 31.32) * mm});
            skLineSegment(sketch, "E339", {"start": v(-110.44, 31.32) * mm, "end": v(-111.25, 32.18) * mm});
            skLineSegment(sketch, "E340", {"start": v(-111.25, 32.18) * mm, "end": v(-112.04, 33.09) * mm});
            skLineSegment(sketch, "E341", {"start": v(-112.04, 33.09) * mm, "end": v(-112.8, 34.04) * mm});
            skLineSegment(sketch, "E342", {"start": v(-112.8, 34.04) * mm, "end": v(-113.53, 35.03) * mm});
            skLineSegment(sketch, "E343", {"start": v(-113.53, 35.03) * mm, "end": v(-114.24, 36.06) * mm});
            skLineSegment(sketch, "E344", {"start": v(-114.24, 36.06) * mm, "end": v(-110.74, 42.16) * mm});
            skLineSegment(sketch, "E345", {"start": v(-110.74, 42.16) * mm, "end": v(-109.49, 42.07) * mm});
            skLineSegment(sketch, "E346", {"start": v(-109.49, 42.07) * mm, "end": v(-108.26, 41.93) * mm});
            skLineSegment(sketch, "E347", {"start": v(-108.26, 41.93) * mm, "end": v(-107.06, 41.76) * mm});
            skLineSegment(sketch, "E348", {"start": v(-107.06, 41.76) * mm, "end": v(-105.88, 41.53) * mm});
            skLineSegment(sketch, "E349", {"start": v(-105.88, 41.53) * mm, "end": v(-104.73, 41.27) * mm});
            skLineSegment(sketch, "E350", {"start": v(-104.73, 41.27) * mm, "end": v(-103.61, 40.95) * mm});
            skLineSegment(sketch, "E351", {"start": v(-103.61, 40.95) * mm, "end": v(-102.53, 40.58) * mm});
            skLineSegment(sketch, "E352", {"start": v(-102.53, 40.58) * mm, "end": v(-101.49, 40.15) * mm});
            skLineSegment(sketch, "E353", {"start": v(-101.49, 40.15) * mm, "end": v(-100.99, 39.9) * mm});
            skLineSegment(sketch, "E354", {"start": v(-100.99, 39.9) * mm, "end": v(-100.5, 39.62) * mm});
            skLineSegment(sketch, "E355", {"start": v(-100.5, 39.62) * mm, "end": v(-100.06, 39.78) * mm});
            skLineSegment(sketch, "E356", {"start": v(-100.06, 39.78) * mm, "end": v(-99.72, 39.78) * mm});
            skLineSegment(sketch, "E357", {"start": v(-99.72, 39.78) * mm, "end": v(-99.33, 39.84) * mm});
            skLineSegment(sketch, "E358", {"start": v(-99.33, 39.84) * mm, "end": v(-98.68, 40.27) * mm});
            skLineSegment(sketch, "E359", {"start": v(-98.68, 40.27) * mm, "end": v(-95.27, 44.5) * mm});
            skLineSegment(sketch, "E360", {"start": v(-95.27, 44.5) * mm, "end": v(-95, 45.22) * mm});
            skLineSegment(sketch, "E361", {"start": v(-95, 45.22) * mm, "end": v(-95.02, 45.61) * mm});
            skLineSegment(sketch, "E362", {"start": v(-95.02, 45.61) * mm, "end": v(-95.09, 45.94) * mm});
            skLineSegment(sketch, "E363", {"start": v(-95.09, 45.94) * mm, "end": v(-95.03, 46.42) * mm});
            skLineSegment(sketch, "E364", {"start": v(-95.03, 46.42) * mm, "end": v(-95.4, 46.83) * mm});
            skLineSegment(sketch, "E365", {"start": v(-95.4, 46.83) * mm, "end": v(-95.75, 47.26) * mm});
            skLineSegment(sketch, "E366", {"start": v(-95.75, 47.26) * mm, "end": v(-96.4, 48.19) * mm});
            skLineSegment(sketch, "E367", {"start": v(-96.4, 48.19) * mm, "end": v(-96.99, 49.17) * mm});
            skLineSegment(sketch, "E368", {"start": v(-96.99, 49.17) * mm, "end": v(-97.53, 50.2) * mm});
            skLineSegment(sketch, "E369", {"start": v(-97.53, 50.2) * mm, "end": v(-98.04, 51.26) * mm});
            skLineSegment(sketch, "E370", {"start": v(-98.04, 51.26) * mm, "end": v(-98.5, 52.37) * mm});
            skLineSegment(sketch, "E371", {"start": v(-98.5, 52.37) * mm, "end": v(-98.93, 53.5) * mm});
            skLineSegment(sketch, "E372", {"start": v(-98.93, 53.5) * mm, "end": v(-99.32, 54.67) * mm});
            skLineSegment(sketch, "E373", {"start": v(-99.32, 54.67) * mm, "end": v(-99.68, 55.87) * mm});
            skLineSegment(sketch, "E374", {"start": v(-99.68, 55.87) * mm, "end": v(-94.46, 60.6) * mm});
            skLineSegment(sketch, "E375", {"start": v(-94.46, 60.6) * mm, "end": v(-93.3, 60.12) * mm});
            skLineSegment(sketch, "E376", {"start": v(-93.3, 60.12) * mm, "end": v(-92.18, 59.61) * mm});
            skLineSegment(sketch, "E377", {"start": v(-92.18, 59.61) * mm, "end": v(-91.09, 59.07) * mm});
            skLineSegment(sketch, "E378", {"start": v(-91.09, 59.07) * mm, "end": v(-90.04, 58.5) * mm});
            skLineSegment(sketch, "E379", {"start": v(-90.04, 58.5) * mm, "end": v(-89.03, 57.89) * mm});
            skLineSegment(sketch, "E380", {"start": v(-89.03, 57.89) * mm, "end": v(-88.06, 57.24) * mm});
            skLineSegment(sketch, "E381", {"start": v(-88.06, 57.24) * mm, "end": v(-87.14, 56.55) * mm});
            skLineSegment(sketch, "E382", {"start": v(-87.14, 56.55) * mm, "end": v(-86.29, 55.82) * mm});
            skLineSegment(sketch, "E383", {"start": v(-86.29, 55.82) * mm, "end": v(-85.89, 55.43) * mm});
            skLineSegment(sketch, "E384", {"start": v(-85.89, 55.43) * mm, "end": v(-85.52, 55.01) * mm});
            skLineSegment(sketch, "E385", {"start": v(-85.52, 55.01) * mm, "end": v(-85.04, 55.03) * mm});
            skLineSegment(sketch, "E386", {"start": v(-85.04, 55.03) * mm, "end": v(-84.72, 54.92) * mm});
            skLineSegment(sketch, "E387", {"start": v(-84.72, 54.92) * mm, "end": v(-84.33, 54.86) * mm});
            skLineSegment(sketch, "E388", {"start": v(-84.33, 54.86) * mm, "end": v(-83.58, 55.06) * mm});
            skLineSegment(sketch, "E389", {"start": v(-83.58, 55.06) * mm, "end": v(-79.03, 58.03) * mm});
            skLineSegment(sketch, "E390", {"start": v(-79.03, 58.03) * mm, "end": v(-78.55, 58.64) * mm});
            skLineSegment(sketch, "E391", {"start": v(-78.55, 58.64) * mm, "end": v(-78.44, 59.02) * mm});
            skLineSegment(sketch, "E392", {"start": v(-78.44, 59.02) * mm, "end": v(-78.41, 59.35) * mm});
            skLineSegment(sketch, "E393", {"start": v(-78.41, 59.35) * mm, "end": v(-78.2, 59.79) * mm});
            skLineSegment(sketch, "E394", {"start": v(-78.2, 59.79) * mm, "end": v(-78.44, 60.29) * mm});
            skLineSegment(sketch, "E395", {"start": v(-78.44, 60.29) * mm, "end": v(-78.63, 60.81) * mm});
            skLineSegment(sketch, "E396", {"start": v(-78.63, 60.81) * mm, "end": v(-78.96, 61.9) * mm});
            skLineSegment(sketch, "E397", {"start": v(-78.96, 61.9) * mm, "end": v(-79.22, 63) * mm});
            skLineSegment(sketch, "E398", {"start": v(-79.22, 63) * mm, "end": v(-79.42, 64.15) * mm});
            skLineSegment(sketch, "E399", {"start": v(-79.42, 64.15) * mm, "end": v(-79.57, 65.32) * mm});
            skLineSegment(sketch, "E400", {"start": v(-79.57, 65.32) * mm, "end": v(-79.67, 66.52) * mm});
            skLineSegment(sketch, "E401", {"start": v(-79.67, 66.52) * mm, "end": v(-79.73, 67.73) * mm});
            skLineSegment(sketch, "E402", {"start": v(-79.73, 67.73) * mm, "end": v(-79.74, 68.97) * mm});
            skLineSegment(sketch, "E403", {"start": v(-79.74, 68.97) * mm, "end": v(-79.71, 70.22) * mm});
            skLineSegment(sketch, "E404", {"start": v(-79.71, 70.22) * mm, "end": v(-73.29, 73.1) * mm});
            skLineSegment(sketch, "E405", {"start": v(-73.29, 73.1) * mm, "end": v(-72.33, 72.28) * mm});
            skLineSegment(sketch, "E406", {"start": v(-72.33, 72.28) * mm, "end": v(-71.42, 71.45) * mm});
            skLineSegment(sketch, "E407", {"start": v(-71.42, 71.45) * mm, "end": v(-70.55, 70.6) * mm});
            skLineSegment(sketch, "E408", {"start": v(-70.55, 70.6) * mm, "end": v(-69.73, 69.73) * mm});
            skLineSegment(sketch, "E409", {"start": v(-69.73, 69.73) * mm, "end": v(-68.95, 68.84) * mm});
            skLineSegment(sketch, "E410", {"start": v(-68.95, 68.84) * mm, "end": v(-68.24, 67.92) * mm});
            skLineSegment(sketch, "E411", {"start": v(-68.24, 67.92) * mm, "end": v(-67.58, 66.99) * mm});
            skLineSegment(sketch, "E412", {"start": v(-67.58, 66.99) * mm, "end": v(-66.99, 66.02) * mm});
            skLineSegment(sketch, "E413", {"start": v(-66.99, 66.02) * mm, "end": v(-66.73, 65.53) * mm});
            skLineSegment(sketch, "E414", {"start": v(-66.73, 65.53) * mm, "end": v(-66.5, 65.02) * mm});
            skLineSegment(sketch, "E415", {"start": v(-66.5, 65.02) * mm, "end": v(-66.05, 64.89) * mm});
            skLineSegment(sketch, "E416", {"start": v(-66.05, 64.89) * mm, "end": v(-65.78, 64.69) * mm});
            skLineSegment(sketch, "E417", {"start": v(-65.78, 64.69) * mm, "end": v(-65.43, 64.51) * mm});
            skLineSegment(sketch, "E418", {"start": v(-65.43, 64.51) * mm, "end": v(-64.65, 64.47) * mm});
            skLineSegment(sketch, "E419", {"start": v(-64.65, 64.47) * mm, "end": v(-59.4, 65.9) * mm});
            skLineSegment(sketch, "E420", {"start": v(-59.4, 65.9) * mm, "end": v(-58.75, 66.32) * mm});
            skLineSegment(sketch, "E421", {"start": v(-58.75, 66.32) * mm, "end": v(-58.54, 66.64) * mm});
            skLineSegment(sketch, "E422", {"start": v(-58.54, 66.64) * mm, "end": v(-58.4, 66.95) * mm});
            skLineSegment(sketch, "E423", {"start": v(-58.4, 66.95) * mm, "end": v(-58.08, 67.3) * mm});
            skLineSegment(sketch, "E424", {"start": v(-58.08, 67.3) * mm, "end": v(-58.14, 67.85) * mm});
            skLineSegment(sketch, "E425", {"start": v(-58.14, 67.85) * mm, "end": v(-58.17, 68.4) * mm});
            skLineSegment(sketch, "E426", {"start": v(-58.17, 68.4) * mm, "end": v(-58.14, 69.54) * mm});
            skLineSegment(sketch, "E427", {"start": v(-58.14, 69.54) * mm, "end": v(-58.05, 70.68) * mm});
            skLineSegment(sketch, "E428", {"start": v(-58.05, 70.68) * mm, "end": v(-57.88, 71.83) * mm});
            skLineSegment(sketch, "E429", {"start": v(-57.88, 71.83) * mm, "end": v(-57.67, 72.99) * mm});
            skLineSegment(sketch, "E430", {"start": v(-57.67, 72.99) * mm, "end": v(-57.4, 74.16) * mm});
            skLineSegment(sketch, "E431", {"start": v(-57.4, 74.16) * mm, "end": v(-57.07, 75.33) * mm});
            skLineSegment(sketch, "E432", {"start": v(-57.07, 75.33) * mm, "end": v(-56.7, 76.5) * mm});
            skLineSegment(sketch, "E433", {"start": v(-56.7, 76.5) * mm, "end": v(-56.28, 77.69) * mm});
            skLineSegment(sketch, "E434", {"start": v(-56.28, 77.69) * mm, "end": v(-49.29, 78.44) * mm});
            skLineSegment(sketch, "E435", {"start": v(-49.29, 78.44) * mm, "end": v(-48.63, 77.37) * mm});
            skLineSegment(sketch, "E436", {"start": v(-48.63, 77.37) * mm, "end": v(-48.02, 76.3) * mm});
            skLineSegment(sketch, "E437", {"start": v(-48.02, 76.3) * mm, "end": v(-47.46, 75.22) * mm});
            skLineSegment(sketch, "E438", {"start": v(-47.46, 75.22) * mm, "end": v(-46.94, 74.14) * mm});
            skLineSegment(sketch, "E439", {"start": v(-46.94, 74.14) * mm, "end": v(-46.48, 73.05) * mm});
            skLineSegment(sketch, "E440", {"start": v(-46.48, 73.05) * mm, "end": v(-46.08, 71.96) * mm});
            skLineSegment(sketch, "E441", {"start": v(-46.08, 71.96) * mm, "end": v(-45.74, 70.87) * mm});
            skLineSegment(sketch, "E442", {"start": v(-45.74, 70.87) * mm, "end": v(-45.48, 69.77) * mm});
            skLineSegment(sketch, "E443", {"start": v(-45.48, 69.77) * mm, "end": v(-45.39, 69.22) * mm});
            skLineSegment(sketch, "E444", {"start": v(-45.39, 69.22) * mm, "end": v(-45.33, 68.67) * mm});
            skLineSegment(sketch, "E445", {"start": v(-45.33, 68.67) * mm, "end": v(-44.94, 68.4) * mm});
            skLineSegment(sketch, "E446", {"start": v(-44.94, 68.4) * mm, "end": v(-44.74, 68.12) * mm});
            skLineSegment(sketch, "E447", {"start": v(-44.74, 68.12) * mm, "end": v(-44.46, 67.85) * mm});
            skLineSegment(sketch, "E448", {"start": v(-44.46, 67.85) * mm, "end": v(-43.74, 67.57) * mm});
            skLineSegment(sketch, "E449", {"start": v(-43.74, 67.57) * mm, "end": v(-38.3, 67.3) * mm});
            skLineSegment(sketch, "E450", {"start": v(-38.3, 67.3) * mm, "end": v(-37.56, 67.5) * mm});
            skLineSegment(sketch, "E451", {"start": v(-37.56, 67.5) * mm, "end": v(-37.26, 67.75) * mm});
            skLineSegment(sketch, "E452", {"start": v(-37.26, 67.75) * mm, "end": v(-37.03, 68) * mm});
            skLineSegment(sketch, "E453", {"start": v(-37.03, 68) * mm, "end": v(-36.61, 68.23) * mm});
            skLineSegment(sketch, "E454", {"start": v(-36.61, 68.23) * mm, "end": v(-36.5, 68.77) * mm});
            skLineSegment(sketch, "E455", {"start": v(-36.5, 68.77) * mm, "end": v(-36.35, 69.3) * mm});
            skLineSegment(sketch, "E456", {"start": v(-36.35, 69.3) * mm, "end": v(-35.98, 70.37) * mm});
            skLineSegment(sketch, "E457", {"start": v(-35.98, 70.37) * mm, "end": v(-35.54, 71.43) * mm});
            skLineSegment(sketch, "E458", {"start": v(-35.54, 71.43) * mm, "end": v(-35.03, 72.48) * mm});
            skLineSegment(sketch, "E459", {"start": v(-35.03, 72.48) * mm, "end": v(-34.46, 73.51) * mm});
            skLineSegment(sketch, "E460", {"start": v(-34.46, 73.51) * mm, "end": v(-33.84, 74.54) * mm});
            skLineSegment(sketch, "E461", {"start": v(-33.84, 74.54) * mm, "end": v(-33.17, 75.55) * mm});
            skLineSegment(sketch, "E462", {"start": v(-33.17, 75.55) * mm, "end": v(-32.46, 76.56) * mm});
            skLineSegment(sketch, "E463", {"start": v(-32.46, 76.56) * mm, "end": v(-31.7, 77.55) * mm});
            skLineSegment(sketch, "E464", {"start": v(-31.7, 77.55) * mm, "end": v(-24.81, 76.1) * mm});
            skLineSegment(sketch, "E465", {"start": v(-24.81, 76.1) * mm, "end": v(-24.51, 74.89) * mm});
            skLineSegment(sketch, "E466", {"start": v(-24.51, 74.89) * mm, "end": v(-24.26, 73.68) * mm});
            skLineSegment(sketch, "E467", {"start": v(-24.26, 73.68) * mm, "end": v(-24.06, 72.48) * mm});
            skLineSegment(sketch, "E468", {"start": v(-24.06, 72.48) * mm, "end": v(-23.9, 71.3) * mm});
            skLineSegment(sketch, "E469", {"start": v(-23.9, 71.3) * mm, "end": v(-23.8, 70.11) * mm});
            skLineSegment(sketch, "E470", {"start": v(-23.8, 70.11) * mm, "end": v(-23.76, 68.95) * mm});
            skLineSegment(sketch, "E471", {"start": v(-23.76, 68.95) * mm, "end": v(-23.78, 67.8) * mm});
            skLineSegment(sketch, "E472", {"start": v(-23.78, 67.8) * mm, "end": v(-23.87, 66.68) * mm});
            skLineSegment(sketch, "E473", {"start": v(-23.87, 66.68) * mm, "end": v(-23.95, 66.13) * mm});
            skLineSegment(sketch, "E474", {"start": v(-23.95, 66.13) * mm, "end": v(-24.07, 65.6) * mm});
            skLineSegment(sketch, "E475", {"start": v(-24.07, 65.6) * mm, "end": v(-23.78, 65.21) * mm});
            skLineSegment(sketch, "E476", {"start": v(-23.78, 65.21) * mm, "end": v(-23.67, 64.89) * mm});
            skLineSegment(sketch, "E477", {"start": v(-23.67, 64.89) * mm, "end": v(-23.5, 64.54) * mm});
            skLineSegment(sketch, "E478", {"start": v(-23.5, 64.54) * mm, "end": v(-22.9, 64.05) * mm});
            skLineSegment(sketch, "E479", {"start": v(-22.9, 64.05) * mm, "end": v(-17.81, 62.12) * mm});
            skLineSegment(sketch, "E480", {"start": v(-17.81, 62.12) * mm, "end": v(-17.04, 62.08) * mm});
            skLineSegment(sketch, "E481", {"start": v(-17.04, 62.08) * mm, "end": v(-16.67, 62.22) * mm});
            skLineSegment(sketch, "E482", {"start": v(-16.67, 62.22) * mm, "end": v(-16.38, 62.39) * mm});
            skLineSegment(sketch, "E483", {"start": v(-16.38, 62.39) * mm, "end": v(-15.9, 62.48) * mm});
            skLineSegment(sketch, "E484", {"start": v(-15.9, 62.48) * mm, "end": v(-15.64, 62.96) * mm});
            skLineSegment(sketch, "E485", {"start": v(-15.64, 62.96) * mm, "end": v(-15.33, 63.43) * mm});
            skLineSegment(sketch, "E486", {"start": v(-15.33, 63.43) * mm, "end": v(-14.65, 64.32) * mm});
            skLineSegment(sketch, "E487", {"start": v(-14.65, 64.32) * mm, "end": v(-13.9, 65.2) * mm});
            skLineSegment(sketch, "E488", {"start": v(-13.9, 65.2) * mm, "end": v(-13.1, 66.03) * mm});
            skLineSegment(sketch, "E489", {"start": v(-13.1, 66.03) * mm, "end": v(-12.23, 66.84) * mm});
            skLineSegment(sketch, "E490", {"start": v(-12.23, 66.84) * mm, "end": v(-11.33, 67.62) * mm});
            skLineSegment(sketch, "E491", {"start": v(-11.33, 67.62) * mm, "end": v(-10.38, 68.38) * mm});
            skLineSegment(sketch, "E492", {"start": v(-10.38, 68.38) * mm, "end": v(-9.38, 69.12) * mm});
            skLineSegment(sketch, "E493", {"start": v(-9.38, 69.12) * mm, "end": v(-8.35, 69.83) * mm});
            skLineSegment(sketch, "E494", {"start": v(-8.35, 69.83) * mm, "end": v(-2.25, 66.32) * mm});
            skLineSegment(sketch, "E495", {"start": v(-2.25, 66.32) * mm, "end": v(-2.35, 65.07) * mm});
            skLineSegment(sketch, "E496", {"start": v(-2.35, 65.07) * mm, "end": v(-2.48, 63.85) * mm});
            skLineSegment(sketch, "E497", {"start": v(-2.48, 63.85) * mm, "end": v(-2.66, 62.64) * mm});
            skLineSegment(sketch, "E498", {"start": v(-2.66, 62.64) * mm, "end": v(-2.88, 61.46) * mm});
            skLineSegment(sketch, "E499", {"start": v(-2.88, 61.46) * mm, "end": v(-3.15, 60.31) * mm});
            skLineSegment(sketch, "E500", {"start": v(-3.15, 60.31) * mm, "end": v(-3.46, 59.2) * mm});
            skLineSegment(sketch, "E501", {"start": v(-3.46, 59.2) * mm, "end": v(-3.84, 58.11) * mm});
            skLineSegment(sketch, "E502", {"start": v(-3.84, 58.11) * mm, "end": v(-4.27, 57.07) * mm});
            skLineSegment(sketch, "E503", {"start": v(-4.27, 57.07) * mm, "end": v(-4.52, 56.57) * mm});
            skLineSegment(sketch, "E504", {"start": v(-4.52, 56.57) * mm, "end": v(-4.8, 56.1) * mm});
            skLineSegment(sketch, "E505", {"start": v(-4.8, 56.1) * mm, "end": v(-4.64, 55.64) * mm});
            skLineSegment(sketch, "E506", {"start": v(-4.64, 55.64) * mm, "end": v(-4.64, 55.3) * mm});
            skLineSegment(sketch, "E507", {"start": v(-4.64, 55.3) * mm, "end": v(-4.57, 54.92) * mm});
            skLineSegment(sketch, "E508", {"start": v(-4.57, 54.92) * mm, "end": v(-4.15, 54.27) * mm});
            skLineSegment(sketch, "E509", {"start": v(-4.15, 54.27) * mm, "end": v(0.08, 50.86) * mm});
            skLineSegment(sketch, "E510", {"start": v(0.08, 50.86) * mm, "end": v(0.8, 50.58) * mm});
            skLineSegment(sketch, "E511", {"start": v(0.8, 50.58) * mm, "end": v(1.2, 50.6) * mm});
            skLineSegment(sketch, "E512", {"start": v(1.2, 50.6) * mm, "end": v(1.53, 50.67) * mm});
            skLineSegment(sketch, "E513", {"start": v(1.53, 50.67) * mm, "end": v(2, 50.61) * mm});
            skLineSegment(sketch, "E514", {"start": v(2, 50.61) * mm, "end": v(2.41, 50.99) * mm});
            skLineSegment(sketch, "E515", {"start": v(2.41, 50.99) * mm, "end": v(2.85, 51.33) * mm});
            skLineSegment(sketch, "E516", {"start": v(2.85, 51.33) * mm, "end": v(3.77, 51.98) * mm});
            skLineSegment(sketch, "E517", {"start": v(3.77, 51.98) * mm, "end": v(4.75, 52.57) * mm});
            skLineSegment(sketch, "E518", {"start": v(4.75, 52.57) * mm, "end": v(5.78, 53.12) * mm});
            skLineSegment(sketch, "E519", {"start": v(5.78, 53.12) * mm, "end": v(6.85, 53.62) * mm});
            skLineSegment(sketch, "E520", {"start": v(6.85, 53.62) * mm, "end": v(7.95, 54.09) * mm});
            skLineSegment(sketch, "E521", {"start": v(7.95, 54.09) * mm, "end": v(9.09, 54.52) * mm});
            skLineSegment(sketch, "E522", {"start": v(9.09, 54.52) * mm, "end": v(10.26, 54.9) * mm});
            skLineSegment(sketch, "E523", {"start": v(10.26, 54.9) * mm, "end": v(11.46, 55.27) * mm});
            skLineSegment(sketch, "E524", {"start": v(11.46, 55.27) * mm, "end": v(16.18, 50.05) * mm});
            skLineSegment(sketch, "E525", {"start": v(16.18, 50.05) * mm, "end": v(15.7, 48.89) * mm});
            skLineSegment(sketch, "E526", {"start": v(15.7, 48.89) * mm, "end": v(15.2, 47.76) * mm});
            skLineSegment(sketch, "E527", {"start": v(15.2, 47.76) * mm, "end": v(14.65, 46.67) * mm});
            skLineSegment(sketch, "E528", {"start": v(14.65, 46.67) * mm, "end": v(14.08, 45.62) * mm});
            skLineSegment(sketch, "E529", {"start": v(14.08, 45.62) * mm, "end": v(13.47, 44.61) * mm});
            skLineSegment(sketch, "E530", {"start": v(13.47, 44.61) * mm, "end": v(12.82, 43.64) * mm});
            skLineSegment(sketch, "E531", {"start": v(12.82, 43.64) * mm, "end": v(12.14, 42.73) * mm});
            skLineSegment(sketch, "E532", {"start": v(12.14, 42.73) * mm, "end": v(11.4, 41.87) * mm});
            skLineSegment(sketch, "E533", {"start": v(11.4, 41.87) * mm, "end": v(11.01, 41.47) * mm});
            skLineSegment(sketch, "E534", {"start": v(11.01, 41.47) * mm, "end": v(10.6, 41.1) * mm});
            skLineSegment(sketch, "E535", {"start": v(10.6, 41.1) * mm, "end": v(10.61, 40.63) * mm});
            skLineSegment(sketch, "E536", {"start": v(10.61, 40.63) * mm, "end": v(10.5, 40.3) * mm});
            skLineSegment(sketch, "E537", {"start": v(10.5, 40.3) * mm, "end": v(10.45, 39.92) * mm});
            skLineSegment(sketch, "E538", {"start": v(10.45, 39.92) * mm, "end": v(10.65, 39.17) * mm});
            skLineSegment(sketch, "E539", {"start": v(10.65, 39.17) * mm, "end": v(13.62, 34.62) * mm});
            skLineSegment(sketch, "E540", {"start": v(13.62, 34.62) * mm, "end": v(14.22, 34.13) * mm});
            skLineSegment(sketch, "E541", {"start": v(14.22, 34.13) * mm, "end": v(14.6, 34.03) * mm});
            skLineSegment(sketch, "E542", {"start": v(14.6, 34.03) * mm, "end": v(14.94, 34) * mm});
            skLineSegment(sketch, "E543", {"start": v(14.94, 34) * mm, "end": v(15.37, 33.79) * mm});
            skLineSegment(sketch, "E544", {"start": v(15.37, 33.79) * mm, "end": v(15.87, 34.02) * mm});
            skLineSegment(sketch, "E545", {"start": v(15.87, 34.02) * mm, "end": v(16.4, 34.22) * mm});
            skLineSegment(sketch, "E546", {"start": v(16.4, 34.22) * mm, "end": v(17.47, 34.54) * mm});
            skLineSegment(sketch, "E547", {"start": v(17.47, 34.54) * mm, "end": v(18.6, 34.8) * mm});
            skLineSegment(sketch, "E548", {"start": v(18.6, 34.8) * mm, "end": v(19.74, 35) * mm});
            skLineSegment(sketch, "E549", {"start": v(19.74, 35) * mm, "end": v(20.9, 35.16) * mm});
            skLineSegment(sketch, "E550", {"start": v(20.9, 35.16) * mm, "end": v(22.1, 35.26) * mm});
            skLineSegment(sketch, "E551", {"start": v(22.1, 35.26) * mm, "end": v(23.32, 35.31) * mm});
            skLineSegment(sketch, "E552", {"start": v(23.32, 35.31) * mm, "end": v(24.55, 35.33) * mm});
            skLineSegment(sketch, "E553", {"start": v(24.55, 35.33) * mm, "end": v(25.8, 35.3) * mm});
            skLineSegment(sketch, "E554", {"start": v(25.8, 35.3) * mm, "end": v(28.68, 28.87) * mm});
            skLineSegment(sketch, "E555", {"start": v(28.68, 28.87) * mm, "end": v(27.87, 27.92) * mm});
            skLineSegment(sketch, "E556", {"start": v(27.87, 27.92) * mm, "end": v(27.04, 27) * mm});
            skLineSegment(sketch, "E557", {"start": v(27.04, 27) * mm, "end": v(26.19, 26.14) * mm});
            skLineSegment(sketch, "E558", {"start": v(26.19, 26.14) * mm, "end": v(25.31, 25.31) * mm});
            skLineSegment(sketch, "E559", {"start": v(25.31, 25.31) * mm, "end": v(24.42, 24.54) * mm});
            skLineSegment(sketch, "E560", {"start": v(24.42, 24.54) * mm, "end": v(23.5, 23.82) * mm});
            skLineSegment(sketch, "E561", {"start": v(23.5, 23.82) * mm, "end": v(22.57, 23.16) * mm});
            skLineSegment(sketch, "E562", {"start": v(22.57, 23.16) * mm, "end": v(21.6, 22.57) * mm});
            skLineSegment(sketch, "E563", {"start": v(21.6, 22.57) * mm, "end": v(21.11, 22.31) * mm});
            skLineSegment(sketch, "E564", {"start": v(21.11, 22.31) * mm, "end": v(20.6, 22.1) * mm});
            skLineSegment(sketch, "E565", {"start": v(20.6, 22.1) * mm, "end": v(20.47, 21.63) * mm});
            skLineSegment(sketch, "E566", {"start": v(20.47, 21.63) * mm, "end": v(20.27, 21.36) * mm});
            skLineSegment(sketch, "E567", {"start": v(20.27, 21.36) * mm, "end": v(20.1, 21.01) * mm});
            skLineSegment(sketch, "E568", {"start": v(20.1, 21.01) * mm, "end": v(20.06, 20.23) * mm});
            skLineSegment(sketch, "E569", {"start": v(20.06, 20.23) * mm, "end": v(21.47, 14.99) * mm});
            skLineSegment(sketch, "E570", {"start": v(21.47, 14.99) * mm, "end": v(21.9, 14.34) * mm});
            skLineSegment(sketch, "E571", {"start": v(21.9, 14.34) * mm, "end": v(22.23, 14.13) * mm});
            skLineSegment(sketch, "E572", {"start": v(22.23, 14.13) * mm, "end": v(22.54, 13.99) * mm});
            skLineSegment(sketch, "E573", {"start": v(22.54, 13.99) * mm, "end": v(22.89, 13.66) * mm});
            skLineSegment(sketch, "E574", {"start": v(22.89, 13.66) * mm, "end": v(23.44, 13.72) * mm});
            skLineSegment(sketch, "E575", {"start": v(23.44, 13.72) * mm, "end": v(24, 13.75) * mm});
            skLineSegment(sketch, "E576", {"start": v(24, 13.75) * mm, "end": v(25.12, 13.73) * mm});
            skLineSegment(sketch, "E577", {"start": v(25.12, 13.73) * mm, "end": v(26.26, 13.63) * mm});
            skLineSegment(sketch, "E578", {"start": v(26.26, 13.63) * mm, "end": v(27.41, 13.47) * mm});
            skLineSegment(sketch, "E579", {"start": v(27.41, 13.47) * mm, "end": v(28.57, 13.25) * mm});
            skLineSegment(sketch, "E580", {"start": v(28.57, 13.25) * mm, "end": v(29.74, 12.98) * mm});
            skLineSegment(sketch, "E581", {"start": v(29.74, 12.98) * mm, "end": v(30.91, 12.66) * mm});
            skLineSegment(sketch, "E582", {"start": v(30.91, 12.66) * mm, "end": v(32.1, 12.28) * mm});
            skLineSegment(sketch, "E583", {"start": v(32.1, 12.28) * mm, "end": v(33.27, 11.87) * mm});
            skLineSegment(sketch, "E584", {"start": v(33.27, 11.87) * mm, "end": v(34.02, 4.87) * mm});
            skLineSegment(sketch, "E585", {"start": v(34.02, 4.87) * mm, "end": v(32.96, 4.21) * mm});
            skLineSegment(sketch, "E586", {"start": v(32.96, 4.21) * mm, "end": v(31.89, 3.6) * mm});
            skLineSegment(sketch, "E587", {"start": v(31.89, 3.6) * mm, "end": v(30.8, 3.04) * mm});
            skLineSegment(sketch, "E588", {"start": v(30.8, 3.04) * mm, "end": v(29.72, 2.53) * mm});
            skLineSegment(sketch, "E589", {"start": v(29.72, 2.53) * mm, "end": v(28.64, 2.07) * mm});
            skLineSegment(sketch, "E590", {"start": v(28.64, 2.07) * mm, "end": v(27.54, 1.66) * mm});
            skLineSegment(sketch, "E591", {"start": v(27.54, 1.66) * mm, "end": v(26.45, 1.33) * mm});
            skLineSegment(sketch, "E592", {"start": v(26.45, 1.33) * mm, "end": v(25.35, 1.07) * mm});
            skLineSegment(sketch, "E593", {"start": v(25.35, 1.07) * mm, "end": v(24.8, 0.97) * mm});
            skLineSegment(sketch, "E594", {"start": v(24.8, 0.97) * mm, "end": v(24.25, 0.92) * mm});
            skLineSegment(sketch, "E595", {"start": v(24.25, 0.92) * mm, "end": v(23.98, 0.52) * mm});
            skLineSegment(sketch, "E596", {"start": v(23.98, 0.52) * mm, "end": v(23.7, 0.32) * mm});
            skLineSegment(sketch, "E597", {"start": v(23.7, 0.32) * mm, "end": v(23.43, 0.05) * mm});
            skLineSegment(sketch, "E598", {"start": v(23.43, 0.05) * mm, "end": v(23.15, -0.68) * mm});
            skLineSegment(sketch, "E599", {"start": v(23.15, -0.68) * mm, "end": v(22.88, -6.1) * mm});
            skLineSegment(sketch, "E600", {"start": v(-41.24, 0) * mm, "end": v(-41.35, 0.82) * mm});
            skLineSegment(sketch, "E601", {"start": v(-41.35, 0.82) * mm, "end": v(-41.67, 1.59) * mm});
            skLineSegment(sketch, "E602", {"start": v(-41.67, 1.59) * mm, "end": v(-42.17, 2.25) * mm});
            skLineSegment(sketch, "E603", {"start": v(-42.17, 2.25) * mm, "end": v(-42.83, 2.75) * mm});
            skLineSegment(sketch, "E604", {"start": v(-42.83, 2.75) * mm, "end": v(-43.6, 3.07) * mm});
            skLineSegment(sketch, "E605", {"start": v(-43.6, 3.07) * mm, "end": v(-44.42, 3.18) * mm});
            skLineSegment(sketch, "E606", {"start": v(-44.42, 3.18) * mm, "end": v(-45.24, 3.07) * mm});
            skLineSegment(sketch, "E607", {"start": v(-45.24, 3.07) * mm, "end": v(-46, 2.75) * mm});
            skLineSegment(sketch, "E608", {"start": v(-46, 2.75) * mm, "end": v(-46.66, 2.25) * mm});
            skLineSegment(sketch, "E609", {"start": v(-46.66, 2.25) * mm, "end": v(-47.17, 1.59) * mm});
            skLineSegment(sketch, "E610", {"start": v(-47.17, 1.59) * mm, "end": v(-47.48, 0.82) * mm});
            skLineSegment(sketch, "E611", {"start": v(-47.48, 0.82) * mm, "end": v(-47.6, 0) * mm});
            skLineSegment(sketch, "E612", {"start": v(-47.6, 0) * mm, "end": v(-47.48, -0.82) * mm});
            skLineSegment(sketch, "E613", {"start": v(-47.48, -0.82) * mm, "end": v(-47.17, -1.59) * mm});
            skLineSegment(sketch, "E614", {"start": v(-47.17, -1.59) * mm, "end": v(-46.66, -2.25) * mm});
            skLineSegment(sketch, "E615", {"start": v(-46.66, -2.25) * mm, "end": v(-46, -2.75) * mm});
            skLineSegment(sketch, "E616", {"start": v(-46, -2.75) * mm, "end": v(-45.24, -3.07) * mm});
            skLineSegment(sketch, "E617", {"start": v(-45.24, -3.07) * mm, "end": v(-44.42, -3.18) * mm});
            skLineSegment(sketch, "E618", {"start": v(-44.42, -3.18) * mm, "end": v(-43.6, -3.07) * mm});
            skLineSegment(sketch, "E619", {"start": v(-43.6, -3.07) * mm, "end": v(-42.83, -2.75) * mm});
            skLineSegment(sketch, "E620", {"start": v(-42.83, -2.75) * mm, "end": v(-42.17, -2.25) * mm});
            skLineSegment(sketch, "E621", {"start": v(-42.17, -2.25) * mm, "end": v(-41.67, -1.59) * mm});
            skLineSegment(sketch, "E622", {"start": v(-41.67, -1.59) * mm, "end": v(-41.35, -0.82) * mm});
            skLineSegment(sketch, "E623", {"start": v(-41.35, -0.82) * mm, "end": v(-41.24, 0) * mm});
            skLineSegment(sketch, "E624", {"start": v(51.4, -9.91) * mm, "end": v(51.05, -9.4) * mm});
            skLineSegment(sketch, "E625", {"start": v(51.05, -9.4) * mm, "end": v(50.8, -9.25) * mm});
            skLineSegment(sketch, "E626", {"start": v(50.8, -9.25) * mm, "end": v(50.58, -9.14) * mm});
            skLineSegment(sketch, "E627", {"start": v(50.58, -9.14) * mm, "end": v(50.37, -9.07) * mm});
            skLineSegment(sketch, "E628", {"start": v(50.37, -9.07) * mm, "end": v(50.16, -9.02) * mm});
            skLineSegment(sketch, "E629", {"start": v(50.16, -9.02) * mm, "end": v(49.96, -9) * mm});
            skLineSegment(sketch, "E630", {"start": v(49.96, -9) * mm, "end": v(49.57, -8.96) * mm});
            skLineSegment(sketch, "E631", {"start": v(49.57, -8.96) * mm, "end": v(49.2, -8.97) * mm});
            skLineSegment(sketch, "E632", {"start": v(49.2, -8.97) * mm, "end": v(48.82, -9) * mm});
            skLineSegment(sketch, "E633", {"start": v(48.82, -9) * mm, "end": v(48.1, -9.14) * mm});
            skLineSegment(sketch, "E634", {"start": v(48.1, -9.14) * mm, "end": v(47.38, -9.3) * mm});
            skLineSegment(sketch, "E635", {"start": v(47.38, -9.3) * mm, "end": v(46.63, -9.36) * mm});
            skLineSegment(sketch, "E636", {"start": v(46.63, -9.36) * mm, "end": v(45.87, -9.34) * mm});
            skLineSegment(sketch, "E637", {"start": v(45.87, -9.34) * mm, "end": v(45.09, -9.27) * mm});
            skLineSegment(sketch, "E638", {"start": v(45.09, -9.27) * mm, "end": v(44.3, -9.15) * mm});
            skLineSegment(sketch, "E639", {"start": v(44.3, -9.15) * mm, "end": v(43.5, -8.99) * mm});
            skLineSegment(sketch, "E640", {"start": v(43.5, -8.99) * mm, "end": v(42.7, -8.78) * mm});
            skLineSegment(sketch, "E641", {"start": v(42.7, -8.78) * mm, "end": v(41.9, -8.54) * mm});
            skLineSegment(sketch, "E642", {"start": v(41.9, -8.54) * mm, "end": v(41.08, -8.25) * mm});
            skLineSegment(sketch, "E643", {"start": v(41.08, -8.25) * mm, "end": v(40.27, -7.93) * mm});
            skLineSegment(sketch, "E644", {"start": v(40.27, -7.93) * mm, "end": v(39.45, -7.57) * mm});
            skLineSegment(sketch, "E645", {"start": v(39.45, -7.57) * mm, "end": v(38.77, -0.84) * mm});
            skLineSegment(sketch, "E646", {"start": v(38.77, -0.84) * mm, "end": v(39.5, -0.33) * mm});
            skLineSegment(sketch, "E647", {"start": v(39.5, -0.33) * mm, "end": v(40.23, 0.15) * mm});
            skLineSegment(sketch, "E648", {"start": v(40.23, 0.15) * mm, "end": v(40.97, 0.6) * mm});
            skLineSegment(sketch, "E649", {"start": v(40.97, 0.6) * mm, "end": v(41.72, 1) * mm});
            skLineSegment(sketch, "E650", {"start": v(41.72, 1) * mm, "end": v(42.46, 1.35) * mm});
            skLineSegment(sketch, "E651", {"start": v(42.46, 1.35) * mm, "end": v(43.2, 1.67) * mm});
            skLineSegment(sketch, "E652", {"start": v(43.2, 1.67) * mm, "end": v(43.96, 1.95) * mm});
            skLineSegment(sketch, "E653", {"start": v(43.96, 1.95) * mm, "end": v(44.7, 2.17) * mm});
            skLineSegment(sketch, "E654", {"start": v(44.7, 2.17) * mm, "end": v(45.45, 2.34) * mm});
            skLineSegment(sketch, "E655", {"start": v(45.45, 2.34) * mm, "end": v(46.2, 2.44) * mm});
            skLineSegment(sketch, "E656", {"start": v(46.2, 2.44) * mm, "end": v(46.93, 2.43) * mm});
            skLineSegment(sketch, "E657", {"start": v(46.93, 2.43) * mm, "end": v(47.67, 2.43) * mm});
            skLineSegment(sketch, "E658", {"start": v(47.67, 2.43) * mm, "end": v(48.04, 2.47) * mm});
            skLineSegment(sketch, "E659", {"start": v(48.04, 2.47) * mm, "end": v(48.41, 2.54) * mm});
            skLineSegment(sketch, "E660", {"start": v(48.41, 2.54) * mm, "end": v(48.79, 2.65) * mm});
            skLineSegment(sketch, "E661", {"start": v(48.79, 2.65) * mm, "end": v(48.98, 2.72) * mm});
            skLineSegment(sketch, "E662", {"start": v(48.98, 2.72) * mm, "end": v(49.17, 2.8) * mm});
            skLineSegment(sketch, "E663", {"start": v(49.17, 2.8) * mm, "end": v(49.37, 2.92) * mm});
            skLineSegment(sketch, "E664", {"start": v(49.37, 2.92) * mm, "end": v(49.56, 3.07) * mm});
            skLineSegment(sketch, "E665", {"start": v(49.56, 3.07) * mm, "end": v(49.77, 3.27) * mm});
            skLineSegment(sketch, "E666", {"start": v(49.77, 3.27) * mm, "end": v(50.02, 3.84) * mm});
            skLineSegment(sketch, "E667", {"start": v(50.02, 3.84) * mm, "end": v(50.49, 6.58) * mm});
            skLineSegment(sketch, "E668", {"start": v(50.49, 6.58) * mm, "end": v(51.2, 9.27) * mm});
            skLineSegment(sketch, "E669", {"start": v(51.2, 9.27) * mm, "end": v(51.2, 9.88) * mm});
            skLineSegment(sketch, "E670", {"start": v(51.2, 9.88) * mm, "end": v(51.1, 10.16) * mm});
            skLineSegment(sketch, "E671", {"start": v(51.1, 10.16) * mm, "end": v(50.98, 10.37) * mm});
            skLineSegment(sketch, "E672", {"start": v(50.98, 10.37) * mm, "end": v(50.85, 10.56) * mm});
            skLineSegment(sketch, "E673", {"start": v(50.85, 10.56) * mm, "end": v(50.71, 10.72) * mm});
            skLineSegment(sketch, "E674", {"start": v(50.71, 10.72) * mm, "end": v(50.57, 10.86) * mm});
            skLineSegment(sketch, "E675", {"start": v(50.57, 10.86) * mm, "end": v(50.27, 11.11) * mm});
            skLineSegment(sketch, "E676", {"start": v(50.27, 11.11) * mm, "end": v(49.96, 11.33) * mm});
            skLineSegment(sketch, "E677", {"start": v(49.96, 11.33) * mm, "end": v(49.64, 11.52) * mm});
            skLineSegment(sketch, "E678", {"start": v(49.64, 11.52) * mm, "end": v(48.97, 11.83) * mm});
            skLineSegment(sketch, "E679", {"start": v(48.97, 11.83) * mm, "end": v(48.3, 12.12) * mm});
            skLineSegment(sketch, "E680", {"start": v(48.3, 12.12) * mm, "end": v(47.66, 12.52) * mm});
            skLineSegment(sketch, "E681", {"start": v(47.66, 12.52) * mm, "end": v(47.05, 12.99) * mm});
            skLineSegment(sketch, "E682", {"start": v(47.05, 12.99) * mm, "end": v(46.46, 13.5) * mm});
            skLineSegment(sketch, "E683", {"start": v(46.46, 13.5) * mm, "end": v(45.9, 14.06) * mm});
            skLineSegment(sketch, "E684", {"start": v(45.9, 14.06) * mm, "end": v(45.35, 14.66) * mm});
            skLineSegment(sketch, "E685", {"start": v(45.35, 14.66) * mm, "end": v(44.82, 15.3) * mm});
            skLineSegment(sketch, "E686", {"start": v(44.82, 15.3) * mm, "end": v(44.3, 15.97) * mm});
            skLineSegment(sketch, "E687", {"start": v(44.3, 15.97) * mm, "end": v(43.82, 16.68) * mm});
            skLineSegment(sketch, "E688", {"start": v(43.82, 16.68) * mm, "end": v(43.35, 17.42) * mm});
            skLineSegment(sketch, "E689", {"start": v(43.35, 17.42) * mm, "end": v(42.9, 18.19) * mm});
            skLineSegment(sketch, "E690", {"start": v(42.9, 18.19) * mm, "end": v(46.3, 24.03) * mm});
            skLineSegment(sketch, "E691", {"start": v(46.3, 24.03) * mm, "end": v(47.2, 24.02) * mm});
            skLineSegment(sketch, "E692", {"start": v(47.2, 24.02) * mm, "end": v(48.07, 23.97) * mm});
            skLineSegment(sketch, "E693", {"start": v(48.07, 23.97) * mm, "end": v(48.93, 23.9) * mm});
            skLineSegment(sketch, "E694", {"start": v(48.93, 23.9) * mm, "end": v(49.77, 23.78) * mm});
            skLineSegment(sketch, "E695", {"start": v(49.77, 23.78) * mm, "end": v(50.58, 23.64) * mm});
            skLineSegment(sketch, "E696", {"start": v(50.58, 23.64) * mm, "end": v(51.37, 23.46) * mm});
            skLineSegment(sketch, "E697", {"start": v(51.37, 23.46) * mm, "end": v(52.14, 23.24) * mm});
            skLineSegment(sketch, "E698", {"start": v(52.14, 23.24) * mm, "end": v(52.88, 22.98) * mm});
            skLineSegment(sketch, "E699", {"start": v(52.88, 22.98) * mm, "end": v(53.58, 22.68) * mm});
            skLineSegment(sketch, "E700", {"start": v(53.58, 22.68) * mm, "end": v(54.24, 22.32) * mm});
            skLineSegment(sketch, "E701", {"start": v(54.24, 22.32) * mm, "end": v(54.83, 21.88) * mm});
            skLineSegment(sketch, "E702", {"start": v(54.83, 21.88) * mm, "end": v(55.43, 21.45) * mm});
            skLineSegment(sketch, "E703", {"start": v(55.43, 21.45) * mm, "end": v(55.75, 21.27) * mm});
            skLineSegment(sketch, "E704", {"start": v(55.75, 21.27) * mm, "end": v(56.1, 21.1) * mm});
            skLineSegment(sketch, "E705", {"start": v(56.1, 21.1) * mm, "end": v(56.46, 20.97) * mm});
            skLineSegment(sketch, "E706", {"start": v(56.46, 20.97) * mm, "end": v(56.66, 20.91) * mm});
            skLineSegment(sketch, "E707", {"start": v(56.66, 20.91) * mm, "end": v(56.87, 20.87) * mm});
            skLineSegment(sketch, "E708", {"start": v(56.87, 20.87) * mm, "end": v(57.09, 20.85) * mm});
            skLineSegment(sketch, "E709", {"start": v(57.09, 20.85) * mm, "end": v(57.33, 20.85) * mm});
            skLineSegment(sketch, "E710", {"start": v(57.33, 20.85) * mm, "end": v(57.62, 20.9) * mm});
            skLineSegment(sketch, "E711", {"start": v(57.62, 20.9) * mm, "end": v(58.16, 21.2) * mm});
            skLineSegment(sketch, "E712", {"start": v(58.16, 21.2) * mm, "end": v(60.15, 23.15) * mm});
            skLineSegment(sketch, "E713", {"start": v(60.15, 23.15) * mm, "end": v(62.3, 24.9) * mm});
            skLineSegment(sketch, "E714", {"start": v(62.3, 24.9) * mm, "end": v(62.67, 25.4) * mm});
            skLineSegment(sketch, "E715", {"start": v(62.67, 25.4) * mm, "end": v(62.75, 25.68) * mm});
            skLineSegment(sketch, "E716", {"start": v(62.75, 25.68) * mm, "end": v(62.78, 25.93) * mm});
            skLineSegment(sketch, "E717", {"start": v(62.78, 25.93) * mm, "end": v(62.78, 26.15) * mm});
            skLineSegment(sketch, "E718", {"start": v(62.78, 26.15) * mm, "end": v(62.76, 26.36) * mm});
            skLineSegment(sketch, "E719", {"start": v(62.76, 26.36) * mm, "end": v(62.73, 26.56) * mm});
            skLineSegment(sketch, "E720", {"start": v(62.73, 26.56) * mm, "end": v(62.64, 26.94) * mm});
            skLineSegment(sketch, "E721", {"start": v(62.64, 26.94) * mm, "end": v(62.51, 27.3) * mm});
            skLineSegment(sketch, "E722", {"start": v(62.51, 27.3) * mm, "end": v(62.36, 27.64) * mm});
            skLineSegment(sketch, "E723", {"start": v(62.36, 27.64) * mm, "end": v(62, 28.29) * mm});
            skLineSegment(sketch, "E724", {"start": v(62, 28.29) * mm, "end": v(61.63, 28.92) * mm});
            skLineSegment(sketch, "E725", {"start": v(61.63, 28.92) * mm, "end": v(61.35, 29.62) * mm});
            skLineSegment(sketch, "E726", {"start": v(61.35, 29.62) * mm, "end": v(61.13, 30.35) * mm});
            skLineSegment(sketch, "E727", {"start": v(61.13, 30.35) * mm, "end": v(60.96, 31.11) * mm});
            skLineSegment(sketch, "E728", {"start": v(60.96, 31.11) * mm, "end": v(60.83, 31.9) * mm});
            skLineSegment(sketch, "E729", {"start": v(60.83, 31.9) * mm, "end": v(60.74, 32.7) * mm});
            skLineSegment(sketch, "E730", {"start": v(60.74, 32.7) * mm, "end": v(60.69, 33.53) * mm});
            skLineSegment(sketch, "E731", {"start": v(60.69, 33.53) * mm, "end": v(60.67, 34.38) * mm});
            skLineSegment(sketch, "E732", {"start": v(60.67, 34.38) * mm, "end": v(60.69, 35.24) * mm});
            skLineSegment(sketch, "E733", {"start": v(60.69, 35.24) * mm, "end": v(60.74, 36.11) * mm});
            skLineSegment(sketch, "E734", {"start": v(60.74, 36.11) * mm, "end": v(60.83, 37) * mm});
            skLineSegment(sketch, "E735", {"start": v(60.83, 37) * mm, "end": v(67.02, 39.72) * mm});
            skLineSegment(sketch, "E736", {"start": v(67.02, 39.72) * mm, "end": v(67.73, 39.19) * mm});
            skLineSegment(sketch, "E737", {"start": v(67.73, 39.19) * mm, "end": v(68.42, 38.64) * mm});
            skLineSegment(sketch, "E738", {"start": v(68.42, 38.64) * mm, "end": v(69.06, 38.07) * mm});
            skLineSegment(sketch, "E739", {"start": v(69.06, 38.07) * mm, "end": v(69.68, 37.5) * mm});
            skLineSegment(sketch, "E740", {"start": v(69.68, 37.5) * mm, "end": v(70.25, 36.9) * mm});
            skLineSegment(sketch, "E741", {"start": v(70.25, 36.9) * mm, "end": v(70.78, 36.28) * mm});
            skLineSegment(sketch, "E742", {"start": v(70.78, 36.28) * mm, "end": v(71.28, 35.65) * mm});
            skLineSegment(sketch, "E743", {"start": v(71.28, 35.65) * mm, "end": v(71.72, 35.01) * mm});
            skLineSegment(sketch, "E744", {"start": v(71.72, 35.01) * mm, "end": v(72.11, 34.35) * mm});
            skLineSegment(sketch, "E745", {"start": v(72.11, 34.35) * mm, "end": v(72.44, 33.68) * mm});
            skLineSegment(sketch, "E746", {"start": v(72.44, 33.68) * mm, "end": v(72.65, 32.97) * mm});
            skLineSegment(sketch, "E747", {"start": v(72.65, 32.97) * mm, "end": v(72.89, 32.28) * mm});
            skLineSegment(sketch, "E748", {"start": v(72.89, 32.28) * mm, "end": v(73.04, 31.94) * mm});
            skLineSegment(sketch, "E749", {"start": v(73.04, 31.94) * mm, "end": v(73.22, 31.6) * mm});
            skLineSegment(sketch, "E750", {"start": v(73.22, 31.6) * mm, "end": v(73.44, 31.28) * mm});
            skLineSegment(sketch, "E751", {"start": v(73.44, 31.28) * mm, "end": v(73.56, 31.12) * mm});
            skLineSegment(sketch, "E752", {"start": v(73.56, 31.12) * mm, "end": v(73.7, 30.96) * mm});
            skLineSegment(sketch, "E753", {"start": v(73.7, 30.96) * mm, "end": v(73.87, 30.81) * mm});
            skLineSegment(sketch, "E754", {"start": v(73.87, 30.81) * mm, "end": v(74.07, 30.67) * mm});
            skLineSegment(sketch, "E755", {"start": v(74.07, 30.67) * mm, "end": v(74.34, 30.54) * mm});
            skLineSegment(sketch, "E756", {"start": v(74.34, 30.54) * mm, "end": v(74.95, 30.47) * mm});
            skLineSegment(sketch, "E757", {"start": v(74.95, 30.47) * mm, "end": v(77.7, 30.88) * mm});
            skLineSegment(sketch, "E758", {"start": v(77.7, 30.88) * mm, "end": v(80.47, 31.03) * mm});
            skLineSegment(sketch, "E759", {"start": v(80.47, 31.03) * mm, "end": v(81.06, 31.22) * mm});
            skLineSegment(sketch, "E760", {"start": v(81.06, 31.22) * mm, "end": v(81.3, 31.4) * mm});
            skLineSegment(sketch, "E761", {"start": v(81.3, 31.4) * mm, "end": v(81.46, 31.58) * mm});
            skLineSegment(sketch, "E762", {"start": v(81.46, 31.58) * mm, "end": v(81.6, 31.76) * mm});
            skLineSegment(sketch, "E763", {"start": v(81.6, 31.76) * mm, "end": v(81.7, 31.94) * mm});
            skLineSegment(sketch, "E764", {"start": v(81.7, 31.94) * mm, "end": v(81.8, 32.12) * mm});
            skLineSegment(sketch, "E765", {"start": v(81.8, 32.12) * mm, "end": v(81.95, 32.48) * mm});
            skLineSegment(sketch, "E766", {"start": v(81.95, 32.48) * mm, "end": v(82.06, 32.85) * mm});
            skLineSegment(sketch, "E767", {"start": v(82.06, 32.85) * mm, "end": v(82.14, 33.2) * mm});
            skLineSegment(sketch, "E768", {"start": v(82.14, 33.2) * mm, "end": v(82.23, 33.94) * mm});
            skLineSegment(sketch, "E769", {"start": v(82.23, 33.94) * mm, "end": v(82.3, 34.67) * mm});
            skLineSegment(sketch, "E770", {"start": v(82.3, 34.67) * mm, "end": v(82.48, 35.4) * mm});
            skLineSegment(sketch, "E771", {"start": v(82.48, 35.4) * mm, "end": v(82.73, 36.12) * mm});
            skLineSegment(sketch, "E772", {"start": v(82.73, 36.12) * mm, "end": v(83.04, 36.84) * mm});
            skLineSegment(sketch, "E773", {"start": v(83.04, 36.84) * mm, "end": v(83.4, 37.55) * mm});
            skLineSegment(sketch, "E774", {"start": v(83.4, 37.55) * mm, "end": v(83.8, 38.26) * mm});
            skLineSegment(sketch, "E775", {"start": v(83.8, 38.26) * mm, "end": v(84.24, 38.96) * mm});
            skLineSegment(sketch, "E776", {"start": v(84.24, 38.96) * mm, "end": v(84.72, 39.65) * mm});
            skLineSegment(sketch, "E777", {"start": v(84.72, 39.65) * mm, "end": v(85.24, 40.34) * mm});
            skLineSegment(sketch, "E778", {"start": v(85.24, 40.34) * mm, "end": v(85.8, 41.01) * mm});
            skLineSegment(sketch, "E779", {"start": v(85.8, 41.01) * mm, "end": v(86.4, 41.68) * mm});
            skLineSegment(sketch, "E780", {"start": v(86.4, 41.68) * mm, "end": v(93, 40.24) * mm});
            skLineSegment(sketch, "E781", {"start": v(93, 40.24) * mm, "end": v(93.27, 39.4) * mm});
            skLineSegment(sketch, "E782", {"start": v(93.27, 39.4) * mm, "end": v(93.5, 38.55) * mm});
            skLineSegment(sketch, "E783", {"start": v(93.5, 38.55) * mm, "end": v(93.69, 37.7) * mm});
            skLineSegment(sketch, "E784", {"start": v(93.69, 37.7) * mm, "end": v(93.84, 36.88) * mm});
            skLineSegment(sketch, "E785", {"start": v(93.84, 36.88) * mm, "end": v(93.95, 36.06) * mm});
            skLineSegment(sketch, "E786", {"start": v(93.95, 36.06) * mm, "end": v(94.02, 35.25) * mm});
            skLineSegment(sketch, "E787", {"start": v(94.02, 35.25) * mm, "end": v(94.05, 34.45) * mm});
            skLineSegment(sketch, "E788", {"start": v(94.05, 34.45) * mm, "end": v(94.04, 33.67) * mm});
            skLineSegment(sketch, "E789", {"start": v(94.04, 33.67) * mm, "end": v(93.97, 32.9) * mm});
            skLineSegment(sketch, "E790", {"start": v(93.97, 32.9) * mm, "end": v(93.83, 32.17) * mm});
            skLineSegment(sketch, "E791", {"start": v(93.83, 32.17) * mm, "end": v(93.6, 31.48) * mm});
            skLineSegment(sketch, "E792", {"start": v(93.6, 31.48) * mm, "end": v(93.37, 30.77) * mm});
            skLineSegment(sketch, "E793", {"start": v(93.37, 30.77) * mm, "end": v(93.3, 30.4) * mm});
            skLineSegment(sketch, "E794", {"start": v(93.3, 30.4) * mm, "end": v(93.24, 30.03) * mm});
            skLineSegment(sketch, "E795", {"start": v(93.24, 30.03) * mm, "end": v(93.23, 29.64) * mm});
            skLineSegment(sketch, "E796", {"start": v(93.23, 29.64) * mm, "end": v(93.24, 29.44) * mm});
            skLineSegment(sketch, "E797", {"start": v(93.24, 29.44) * mm, "end": v(93.26, 29.23) * mm});
            skLineSegment(sketch, "E798", {"start": v(93.26, 29.23) * mm, "end": v(93.3, 29) * mm});
            skLineSegment(sketch, "E799", {"start": v(93.3, 29) * mm, "end": v(93.39, 28.77) * mm});
            skLineSegment(sketch, "E800", {"start": v(93.39, 28.77) * mm, "end": v(93.52, 28.51) * mm});
            skLineSegment(sketch, "E801", {"start": v(93.52, 28.51) * mm, "end": v(93.98, 28.1) * mm});
            skLineSegment(sketch, "E802", {"start": v(93.98, 28.1) * mm, "end": v(96.44, 26.8) * mm});
            skLineSegment(sketch, "E803", {"start": v(96.44, 26.8) * mm, "end": v(98.78, 25.3) * mm});
            skLineSegment(sketch, "E804", {"start": v(98.78, 25.3) * mm, "end": v(99.36, 25.1) * mm});
            skLineSegment(sketch, "E805", {"start": v(99.36, 25.1) * mm, "end": v(99.66, 25.12) * mm});
            skLineSegment(sketch, "E806", {"start": v(99.66, 25.12) * mm, "end": v(99.9, 25.17) * mm});
            skLineSegment(sketch, "E807", {"start": v(99.9, 25.17) * mm, "end": v(100.11, 25.23) * mm});
            skLineSegment(sketch, "E808", {"start": v(100.11, 25.23) * mm, "end": v(100.3, 25.32) * mm});
            skLineSegment(sketch, "E809", {"start": v(100.3, 25.32) * mm, "end": v(100.49, 25.4) * mm});
            skLineSegment(sketch, "E810", {"start": v(100.49, 25.4) * mm, "end": v(100.82, 25.61) * mm});
            skLineSegment(sketch, "E811", {"start": v(100.82, 25.61) * mm, "end": v(101.12, 25.84) * mm});
            skLineSegment(sketch, "E812", {"start": v(101.12, 25.84) * mm, "end": v(101.4, 26.09) * mm});
            skLineSegment(sketch, "E813", {"start": v(101.4, 26.09) * mm, "end": v(101.9, 26.63) * mm});
            skLineSegment(sketch, "E814", {"start": v(101.9, 26.63) * mm, "end": v(102.4, 27.18) * mm});
            skLineSegment(sketch, "E815", {"start": v(102.4, 27.18) * mm, "end": v(102.97, 27.66) * mm});
            skLineSegment(sketch, "E816", {"start": v(102.97, 27.66) * mm, "end": v(103.6, 28.1) * mm});
            skLineSegment(sketch, "E817", {"start": v(103.6, 28.1) * mm, "end": v(104.27, 28.5) * mm});
            skLineSegment(sketch, "E818", {"start": v(104.27, 28.5) * mm, "end": v(104.98, 28.86) * mm});
            skLineSegment(sketch, "E819", {"start": v(104.98, 28.86) * mm, "end": v(105.72, 29.2) * mm});
            skLineSegment(sketch, "E820", {"start": v(105.72, 29.2) * mm, "end": v(106.49, 29.5) * mm});
            skLineSegment(sketch, "E821", {"start": v(106.49, 29.5) * mm, "end": v(107.28, 29.78) * mm});
            skLineSegment(sketch, "E822", {"start": v(107.28, 29.78) * mm, "end": v(108.1, 30.03) * mm});
            skLineSegment(sketch, "E823", {"start": v(108.1, 30.03) * mm, "end": v(108.96, 30.25) * mm});
            skLineSegment(sketch, "E824", {"start": v(108.96, 30.25) * mm, "end": v(109.83, 30.43) * mm});
            skLineSegment(sketch, "E825", {"start": v(109.83, 30.43) * mm, "end": v(114.33, 25.4) * mm});
            skLineSegment(sketch, "E826", {"start": v(114.33, 25.4) * mm, "end": v(114.04, 24.55) * mm});
            skLineSegment(sketch, "E827", {"start": v(114.04, 24.55) * mm, "end": v(113.73, 23.73) * mm});
            skLineSegment(sketch, "E828", {"start": v(113.73, 23.73) * mm, "end": v(113.4, 22.94) * mm});
            skLineSegment(sketch, "E829", {"start": v(113.4, 22.94) * mm, "end": v(113.03, 22.18) * mm});
            skLineSegment(sketch, "E830", {"start": v(113.03, 22.18) * mm, "end": v(112.64, 21.45) * mm});
            skLineSegment(sketch, "E831", {"start": v(112.64, 21.45) * mm, "end": v(112.22, 20.75) * mm});
            skLineSegment(sketch, "E832", {"start": v(112.22, 20.75) * mm, "end": v(111.78, 20.09) * mm});
            skLineSegment(sketch, "E833", {"start": v(111.78, 20.09) * mm, "end": v(111.3, 19.47) * mm});
            skLineSegment(sketch, "E834", {"start": v(111.3, 19.47) * mm, "end": v(110.8, 18.9) * mm});
            skLineSegment(sketch, "E835", {"start": v(110.8, 18.9) * mm, "end": v(110.26, 18.37) * mm});
            skLineSegment(sketch, "E836", {"start": v(110.26, 18.37) * mm, "end": v(109.65, 17.95) * mm});
            skLineSegment(sketch, "E837", {"start": v(109.65, 17.95) * mm, "end": v(109.06, 17.51) * mm});
            skLineSegment(sketch, "E838", {"start": v(109.06, 17.51) * mm, "end": v(108.78, 17.26) * mm});
            skLineSegment(sketch, "E839", {"start": v(108.78, 17.26) * mm, "end": v(108.52, 16.99) * mm});
            skLineSegment(sketch, "E840", {"start": v(108.52, 16.99) * mm, "end": v(108.28, 16.68) * mm});
            skLineSegment(sketch, "E841", {"start": v(108.28, 16.68) * mm, "end": v(108.17, 16.51) * mm});
            skLineSegment(sketch, "E842", {"start": v(108.17, 16.51) * mm, "end": v(108.06, 16.33) * mm});
            skLineSegment(sketch, "E843", {"start": v(108.06, 16.33) * mm, "end": v(107.97, 16.12) * mm});
            skLineSegment(sketch, "E844", {"start": v(107.97, 16.12) * mm, "end": v(107.9, 15.89) * mm});
            skLineSegment(sketch, "E845", {"start": v(107.9, 15.89) * mm, "end": v(107.85, 15.6) * mm});
            skLineSegment(sketch, "E846", {"start": v(107.85, 15.6) * mm, "end": v(107.98, 15) * mm});
            skLineSegment(sketch, "E847", {"start": v(107.98, 15) * mm, "end": v(109.22, 12.5) * mm});
            skLineSegment(sketch, "E848", {"start": v(109.22, 12.5) * mm, "end": v(110.22, 9.91) * mm});
            skLineSegment(sketch, "E849", {"start": v(110.22, 9.91) * mm, "end": v(110.58, 9.4) * mm});
            skLineSegment(sketch, "E850", {"start": v(110.58, 9.4) * mm, "end": v(110.82, 9.25) * mm});
            skLineSegment(sketch, "E851", {"start": v(110.82, 9.25) * mm, "end": v(111.04, 9.14) * mm});
            skLineSegment(sketch, "E852", {"start": v(111.04, 9.14) * mm, "end": v(111.26, 9.07) * mm});
            skLineSegment(sketch, "E853", {"start": v(111.26, 9.07) * mm, "end": v(111.46, 9.02) * mm});
            skLineSegment(sketch, "E854", {"start": v(111.46, 9.02) * mm, "end": v(111.66, 9) * mm});
            skLineSegment(sketch, "E855", {"start": v(111.66, 9) * mm, "end": v(112.06, 8.96) * mm});
            skLineSegment(sketch, "E856", {"start": v(112.06, 8.96) * mm, "end": v(112.44, 8.97) * mm});
            skLineSegment(sketch, "E857", {"start": v(112.44, 8.97) * mm, "end": v(112.8, 9) * mm});
            skLineSegment(sketch, "E858", {"start": v(112.8, 9) * mm, "end": v(113.53, 9.14) * mm});
            skLineSegment(sketch, "E859", {"start": v(113.53, 9.14) * mm, "end": v(114.25, 9.3) * mm});
            skLineSegment(sketch, "E860", {"start": v(114.25, 9.3) * mm, "end": v(115, 9.36) * mm});
            skLineSegment(sketch, "E861", {"start": v(115, 9.36) * mm, "end": v(115.76, 9.34) * mm});
            skLineSegment(sketch, "E862", {"start": v(115.76, 9.34) * mm, "end": v(116.54, 9.27) * mm});
            skLineSegment(sketch, "E863", {"start": v(116.54, 9.27) * mm, "end": v(117.33, 9.15) * mm});
            skLineSegment(sketch, "E864", {"start": v(117.33, 9.15) * mm, "end": v(118.12, 8.99) * mm});
            skLineSegment(sketch, "E865", {"start": v(118.12, 8.99) * mm, "end": v(118.93, 8.78) * mm});
            skLineSegment(sketch, "E866", {"start": v(118.93, 8.78) * mm, "end": v(119.73, 8.54) * mm});
            skLineSegment(sketch, "E867", {"start": v(119.73, 8.54) * mm, "end": v(120.55, 8.25) * mm});
            skLineSegment(sketch, "E868", {"start": v(120.55, 8.25) * mm, "end": v(121.36, 7.93) * mm});
            skLineSegment(sketch, "E869", {"start": v(121.36, 7.93) * mm, "end": v(122.18, 7.57) * mm});
            skLineSegment(sketch, "E870", {"start": v(122.18, 7.57) * mm, "end": v(122.85, 0.84) * mm});
            skLineSegment(sketch, "E871", {"start": v(122.85, 0.84) * mm, "end": v(122.13, 0.33) * mm});
            skLineSegment(sketch, "E872", {"start": v(122.13, 0.33) * mm, "end": v(121.4, -0.15) * mm});
            skLineSegment(sketch, "E873", {"start": v(121.4, -0.15) * mm, "end": v(120.65, -0.6) * mm});
            skLineSegment(sketch, "E874", {"start": v(120.65, -0.6) * mm, "end": v(119.91, -1) * mm});
            skLineSegment(sketch, "E875", {"start": v(119.91, -1) * mm, "end": v(119.17, -1.35) * mm});
            skLineSegment(sketch, "E876", {"start": v(119.17, -1.35) * mm, "end": v(118.42, -1.67) * mm});
            skLineSegment(sketch, "E877", {"start": v(118.42, -1.67) * mm, "end": v(117.67, -1.95) * mm});
            skLineSegment(sketch, "E878", {"start": v(117.67, -1.95) * mm, "end": v(116.92, -2.17) * mm});
            skLineSegment(sketch, "E879", {"start": v(116.92, -2.17) * mm, "end": v(116.18, -2.34) * mm});
            skLineSegment(sketch, "E880", {"start": v(116.18, -2.34) * mm, "end": v(115.43, -2.44) * mm});
            skLineSegment(sketch, "E881", {"start": v(115.43, -2.44) * mm, "end": v(114.7, -2.43) * mm});
            skLineSegment(sketch, "E882", {"start": v(114.7, -2.43) * mm, "end": v(113.96, -2.43) * mm});
            skLineSegment(sketch, "E883", {"start": v(113.96, -2.43) * mm, "end": v(113.59, -2.47) * mm});
            skLineSegment(sketch, "E884", {"start": v(113.59, -2.47) * mm, "end": v(113.22, -2.54) * mm});
            skLineSegment(sketch, "E885", {"start": v(113.22, -2.54) * mm, "end": v(112.84, -2.65) * mm});
            skLineSegment(sketch, "E886", {"start": v(112.84, -2.65) * mm, "end": v(112.65, -2.72) * mm});
            skLineSegment(sketch, "E887", {"start": v(112.65, -2.72) * mm, "end": v(112.46, -2.8) * mm});
            skLineSegment(sketch, "E888", {"start": v(112.46, -2.8) * mm, "end": v(112.26, -2.92) * mm});
            skLineSegment(sketch, "E889", {"start": v(112.26, -2.92) * mm, "end": v(112.06, -3.07) * mm});
            skLineSegment(sketch, "E890", {"start": v(112.06, -3.07) * mm, "end": v(111.86, -3.28) * mm});
            skLineSegment(sketch, "E891", {"start": v(111.86, -3.28) * mm, "end": v(111.6, -3.84) * mm});
            skLineSegment(sketch, "E892", {"start": v(111.6, -3.84) * mm, "end": v(111.14, -6.58) * mm});
            skLineSegment(sketch, "E893", {"start": v(111.14, -6.58) * mm, "end": v(110.43, -9.27) * mm});
            skLineSegment(sketch, "E894", {"start": v(110.43, -9.27) * mm, "end": v(110.42, -9.88) * mm});
            skLineSegment(sketch, "E895", {"start": v(110.42, -9.88) * mm, "end": v(110.53, -10.16) * mm});
            skLineSegment(sketch, "E896", {"start": v(110.53, -10.16) * mm, "end": v(110.65, -10.37) * mm});
            skLineSegment(sketch, "E897", {"start": v(110.65, -10.37) * mm, "end": v(110.78, -10.56) * mm});
            skLineSegment(sketch, "E898", {"start": v(110.78, -10.56) * mm, "end": v(110.91, -10.72) * mm});
            skLineSegment(sketch, "E899", {"start": v(110.91, -10.72) * mm, "end": v(111.06, -10.86) * mm});
            skLineSegment(sketch, "E900", {"start": v(111.06, -10.86) * mm, "end": v(111.36, -11.11) * mm});
            skLineSegment(sketch, "E901", {"start": v(111.36, -11.11) * mm, "end": v(111.67, -11.33) * mm});
            skLineSegment(sketch, "E902", {"start": v(111.67, -11.33) * mm, "end": v(111.99, -11.52) * mm});
            skLineSegment(sketch, "E903", {"start": v(111.99, -11.52) * mm, "end": v(112.66, -11.83) * mm});
            skLineSegment(sketch, "E904", {"start": v(112.66, -11.83) * mm, "end": v(113.33, -12.12) * mm});
            skLineSegment(sketch, "E905", {"start": v(113.33, -12.12) * mm, "end": v(113.97, -12.52) * mm});
            skLineSegment(sketch, "E906", {"start": v(113.97, -12.52) * mm, "end": v(114.58, -12.99) * mm});
            skLineSegment(sketch, "E907", {"start": v(114.58, -12.99) * mm, "end": v(115.16, -13.5) * mm});
            skLineSegment(sketch, "E908", {"start": v(115.16, -13.5) * mm, "end": v(115.73, -14.06) * mm});
            skLineSegment(sketch, "E909", {"start": v(115.73, -14.06) * mm, "end": v(116.28, -14.66) * mm});
            skLineSegment(sketch, "E910", {"start": v(116.28, -14.66) * mm, "end": v(116.8, -15.3) * mm});
            skLineSegment(sketch, "E911", {"start": v(116.8, -15.3) * mm, "end": v(117.32, -15.97) * mm});
            skLineSegment(sketch, "E912", {"start": v(117.32, -15.97) * mm, "end": v(117.8, -16.68) * mm});
            skLineSegment(sketch, "E913", {"start": v(117.8, -16.68) * mm, "end": v(118.28, -17.42) * mm});
            skLineSegment(sketch, "E914", {"start": v(118.28, -17.42) * mm, "end": v(118.72, -18.19) * mm});
            skLineSegment(sketch, "E915", {"start": v(118.72, -18.19) * mm, "end": v(115.32, -24.03) * mm});
            skLineSegment(sketch, "E916", {"start": v(115.32, -24.03) * mm, "end": v(114.43, -24.02) * mm});
            skLineSegment(sketch, "E917", {"start": v(114.43, -24.02) * mm, "end": v(113.56, -23.97) * mm});
            skLineSegment(sketch, "E918", {"start": v(113.56, -23.97) * mm, "end": v(112.7, -23.9) * mm});
            skLineSegment(sketch, "E919", {"start": v(112.7, -23.9) * mm, "end": v(111.86, -23.78) * mm});
            skLineSegment(sketch, "E920", {"start": v(111.86, -23.78) * mm, "end": v(111.05, -23.64) * mm});
            skLineSegment(sketch, "E921", {"start": v(111.05, -23.64) * mm, "end": v(110.25, -23.46) * mm});
            skLineSegment(sketch, "E922", {"start": v(110.25, -23.46) * mm, "end": v(109.49, -23.24) * mm});
            skLineSegment(sketch, "E923", {"start": v(109.49, -23.24) * mm, "end": v(108.75, -22.98) * mm});
            skLineSegment(sketch, "E924", {"start": v(108.75, -22.98) * mm, "end": v(108.05, -22.68) * mm});
            skLineSegment(sketch, "E925", {"start": v(108.05, -22.68) * mm, "end": v(107.39, -22.32) * mm});
            skLineSegment(sketch, "E926", {"start": v(107.39, -22.32) * mm, "end": v(106.8, -21.88) * mm});
            skLineSegment(sketch, "E927", {"start": v(106.8, -21.88) * mm, "end": v(106.2, -21.45) * mm});
            skLineSegment(sketch, "E928", {"start": v(106.2, -21.45) * mm, "end": v(105.88, -21.27) * mm});
            skLineSegment(sketch, "E929", {"start": v(105.88, -21.27) * mm, "end": v(105.53, -21.1) * mm});
            skLineSegment(sketch, "E930", {"start": v(105.53, -21.1) * mm, "end": v(105.17, -20.97) * mm});
            skLineSegment(sketch, "E931", {"start": v(105.17, -20.97) * mm, "end": v(104.97, -20.91) * mm});
            skLineSegment(sketch, "E932", {"start": v(104.97, -20.91) * mm, "end": v(104.76, -20.87) * mm});
            skLineSegment(sketch, "E933", {"start": v(104.76, -20.87) * mm, "end": v(104.54, -20.85) * mm});
            skLineSegment(sketch, "E934", {"start": v(104.54, -20.85) * mm, "end": v(104.3, -20.85) * mm});
            skLineSegment(sketch, "E935", {"start": v(104.3, -20.85) * mm, "end": v(104, -20.9) * mm});
            skLineSegment(sketch, "E936", {"start": v(104, -20.9) * mm, "end": v(103.47, -21.2) * mm});
            skLineSegment(sketch, "E937", {"start": v(103.47, -21.2) * mm, "end": v(101.48, -23.15) * mm});
            skLineSegment(sketch, "E938", {"start": v(101.48, -23.15) * mm, "end": v(99.33, -24.9) * mm});
            skLineSegment(sketch, "E939", {"start": v(99.33, -24.9) * mm, "end": v(98.96, -25.4) * mm});
            skLineSegment(sketch, "E940", {"start": v(98.96, -25.4) * mm, "end": v(98.88, -25.68) * mm});
            skLineSegment(sketch, "E941", {"start": v(98.88, -25.68) * mm, "end": v(98.85, -25.93) * mm});
            skLineSegment(sketch, "E942", {"start": v(98.85, -25.93) * mm, "end": v(98.85, -26.15) * mm});
            skLineSegment(sketch, "E943", {"start": v(98.85, -26.15) * mm, "end": v(98.87, -26.36) * mm});
            skLineSegment(sketch, "E944", {"start": v(98.87, -26.36) * mm, "end": v(98.9, -26.56) * mm});
            skLineSegment(sketch, "E945", {"start": v(98.9, -26.56) * mm, "end": v(99, -26.94) * mm});
            skLineSegment(sketch, "E946", {"start": v(99, -26.94) * mm, "end": v(99.12, -27.3) * mm});
            skLineSegment(sketch, "E947", {"start": v(99.12, -27.3) * mm, "end": v(99.26, -27.64) * mm});
            skLineSegment(sketch, "E948", {"start": v(99.26, -27.64) * mm, "end": v(99.62, -28.29) * mm});
            skLineSegment(sketch, "E949", {"start": v(99.62, -28.29) * mm, "end": v(100, -28.92) * mm});
            skLineSegment(sketch, "E950", {"start": v(100, -28.92) * mm, "end": v(100.27, -29.62) * mm});
            skLineSegment(sketch, "E951", {"start": v(100.27, -29.62) * mm, "end": v(100.5, -30.35) * mm});
            skLineSegment(sketch, "E952", {"start": v(100.5, -30.35) * mm, "end": v(100.67, -31.11) * mm});
            skLineSegment(sketch, "E953", {"start": v(100.67, -31.11) * mm, "end": v(100.8, -31.9) * mm});
            skLineSegment(sketch, "E954", {"start": v(100.8, -31.9) * mm, "end": v(100.89, -32.7) * mm});
            skLineSegment(sketch, "E955", {"start": v(100.89, -32.7) * mm, "end": v(100.94, -33.53) * mm});
            skLineSegment(sketch, "E956", {"start": v(100.94, -33.53) * mm, "end": v(100.96, -34.38) * mm});
            skLineSegment(sketch, "E957", {"start": v(100.96, -34.38) * mm, "end": v(100.94, -35.24) * mm});
            skLineSegment(sketch, "E958", {"start": v(100.94, -35.24) * mm, "end": v(100.88, -36.11) * mm});
            skLineSegment(sketch, "E959", {"start": v(100.88, -36.11) * mm, "end": v(100.8, -37) * mm});
            skLineSegment(sketch, "E960", {"start": v(100.8, -37) * mm, "end": v(94.6, -39.72) * mm});
            skLineSegment(sketch, "E961", {"start": v(94.6, -39.72) * mm, "end": v(93.9, -39.19) * mm});
            skLineSegment(sketch, "E962", {"start": v(93.9, -39.19) * mm, "end": v(93.21, -38.64) * mm});
            skLineSegment(sketch, "E963", {"start": v(93.21, -38.64) * mm, "end": v(92.56, -38.07) * mm});
            skLineSegment(sketch, "E964", {"start": v(92.56, -38.07) * mm, "end": v(91.95, -37.5) * mm});
            skLineSegment(sketch, "E965", {"start": v(91.95, -37.5) * mm, "end": v(91.38, -36.9) * mm});
            skLineSegment(sketch, "E966", {"start": v(91.38, -36.9) * mm, "end": v(90.84, -36.28) * mm});
            skLineSegment(sketch, "E967", {"start": v(90.84, -36.28) * mm, "end": v(90.35, -35.65) * mm});
            skLineSegment(sketch, "E968", {"start": v(90.35, -35.65) * mm, "end": v(89.9, -35.01) * mm});
            skLineSegment(sketch, "E969", {"start": v(89.9, -35.01) * mm, "end": v(89.51, -34.35) * mm});
            skLineSegment(sketch, "E970", {"start": v(89.51, -34.35) * mm, "end": v(89.19, -33.68) * mm});
            skLineSegment(sketch, "E971", {"start": v(89.19, -33.68) * mm, "end": v(88.98, -32.98) * mm});
            skLineSegment(sketch, "E972", {"start": v(88.98, -32.98) * mm, "end": v(88.74, -32.28) * mm});
            skLineSegment(sketch, "E973", {"start": v(88.74, -32.28) * mm, "end": v(88.59, -31.94) * mm});
            skLineSegment(sketch, "E974", {"start": v(88.59, -31.94) * mm, "end": v(88.4, -31.6) * mm});
            skLineSegment(sketch, "E975", {"start": v(88.4, -31.6) * mm, "end": v(88.2, -31.28) * mm});
            skLineSegment(sketch, "E976", {"start": v(88.2, -31.28) * mm, "end": v(88.06, -31.12) * mm});
            skLineSegment(sketch, "E977", {"start": v(88.06, -31.12) * mm, "end": v(87.92, -30.96) * mm});
            skLineSegment(sketch, "E978", {"start": v(87.92, -30.96) * mm, "end": v(87.75, -30.81) * mm});
            skLineSegment(sketch, "E979", {"start": v(87.75, -30.81) * mm, "end": v(87.55, -30.67) * mm});
            skLineSegment(sketch, "E980", {"start": v(87.55, -30.67) * mm, "end": v(87.3, -30.54) * mm});
            skLineSegment(sketch, "E981", {"start": v(87.3, -30.54) * mm, "end": v(86.68, -30.47) * mm});
            skLineSegment(sketch, "E982", {"start": v(86.68, -30.47) * mm, "end": v(83.93, -30.88) * mm});
            skLineSegment(sketch, "E983", {"start": v(83.93, -30.88) * mm, "end": v(81.15, -31.03) * mm});
            skLineSegment(sketch, "E984", {"start": v(81.15, -31.03) * mm, "end": v(80.56, -31.22) * mm});
            skLineSegment(sketch, "E985", {"start": v(80.56, -31.22) * mm, "end": v(80.33, -31.4) * mm});
            skLineSegment(sketch, "E986", {"start": v(80.33, -31.4) * mm, "end": v(80.17, -31.58) * mm});
            skLineSegment(sketch, "E987", {"start": v(80.17, -31.58) * mm, "end": v(80.03, -31.76) * mm});
            skLineSegment(sketch, "E988", {"start": v(80.03, -31.76) * mm, "end": v(79.92, -31.94) * mm});
            skLineSegment(sketch, "E989", {"start": v(79.92, -31.94) * mm, "end": v(79.83, -32.12) * mm});
            skLineSegment(sketch, "E990", {"start": v(79.83, -32.12) * mm, "end": v(79.68, -32.48) * mm});
            skLineSegment(sketch, "E991", {"start": v(79.68, -32.48) * mm, "end": v(79.57, -32.85) * mm});
            skLineSegment(sketch, "E992", {"start": v(79.57, -32.85) * mm, "end": v(79.5, -33.2) * mm});
            skLineSegment(sketch, "E993", {"start": v(79.5, -33.2) * mm, "end": v(79.4, -33.94) * mm});
            skLineSegment(sketch, "E994", {"start": v(79.4, -33.94) * mm, "end": v(79.33, -34.67) * mm});
            skLineSegment(sketch, "E995", {"start": v(79.33, -34.67) * mm, "end": v(79.15, -35.4) * mm});
            skLineSegment(sketch, "E996", {"start": v(79.15, -35.4) * mm, "end": v(78.9, -36.12) * mm});
            skLineSegment(sketch, "E997", {"start": v(78.9, -36.12) * mm, "end": v(78.59, -36.84) * mm});
            skLineSegment(sketch, "E998", {"start": v(78.59, -36.84) * mm, "end": v(78.23, -37.55) * mm});
            skLineSegment(sketch, "E999", {"start": v(78.23, -37.55) * mm, "end": v(77.83, -38.26) * mm});
            skLineSegment(sketch, "E1000", {"start": v(77.83, -38.26) * mm, "end": v(77.39, -38.96) * mm});
            skLineSegment(sketch, "E1001", {"start": v(77.39, -38.96) * mm, "end": v(76.9, -39.65) * mm});
            skLineSegment(sketch, "E1002", {"start": v(76.9, -39.65) * mm, "end": v(76.38, -40.34) * mm});
            skLineSegment(sketch, "E1003", {"start": v(76.38, -40.34) * mm, "end": v(75.82, -41.01) * mm});
            skLineSegment(sketch, "E1004", {"start": v(75.82, -41.01) * mm, "end": v(75.23, -41.68) * mm});
            skLineSegment(sketch, "E1005", {"start": v(75.23, -41.68) * mm, "end": v(68.63, -40.24) * mm});
            skLineSegment(sketch, "E1006", {"start": v(68.63, -40.24) * mm, "end": v(68.36, -39.4) * mm});
            skLineSegment(sketch, "E1007", {"start": v(68.36, -39.4) * mm, "end": v(68.13, -38.55) * mm});
            skLineSegment(sketch, "E1008", {"start": v(68.13, -38.55) * mm, "end": v(67.94, -37.7) * mm});
            skLineSegment(sketch, "E1009", {"start": v(67.94, -37.7) * mm, "end": v(67.79, -36.88) * mm});
            skLineSegment(sketch, "E1010", {"start": v(67.79, -36.88) * mm, "end": v(67.67, -36.06) * mm});
            skLineSegment(sketch, "E1011", {"start": v(67.67, -36.06) * mm, "end": v(67.6, -35.25) * mm});
            skLineSegment(sketch, "E1012", {"start": v(67.6, -35.25) * mm, "end": v(67.57, -34.45) * mm});
            skLineSegment(sketch, "E1013", {"start": v(67.57, -34.45) * mm, "end": v(67.6, -33.67) * mm});
            skLineSegment(sketch, "E1014", {"start": v(67.6, -33.67) * mm, "end": v(67.66, -32.9) * mm});
            skLineSegment(sketch, "E1015", {"start": v(67.66, -32.9) * mm, "end": v(67.8, -32.17) * mm});
            skLineSegment(sketch, "E1016", {"start": v(67.8, -32.17) * mm, "end": v(68.04, -31.48) * mm});
            skLineSegment(sketch, "E1017", {"start": v(68.04, -31.48) * mm, "end": v(68.26, -30.77) * mm});
            skLineSegment(sketch, "E1018", {"start": v(68.26, -30.77) * mm, "end": v(68.33, -30.4) * mm});
            skLineSegment(sketch, "E1019", {"start": v(68.33, -30.4) * mm, "end": v(68.38, -30.03) * mm});
            skLineSegment(sketch, "E1020", {"start": v(68.38, -30.03) * mm, "end": v(68.4, -29.64) * mm});
            skLineSegment(sketch, "E1021", {"start": v(68.4, -29.64) * mm, "end": v(68.39, -29.44) * mm});
            skLineSegment(sketch, "E1022", {"start": v(68.39, -29.44) * mm, "end": v(68.36, -29.23) * mm});
            skLineSegment(sketch, "E1023", {"start": v(68.36, -29.23) * mm, "end": v(68.32, -29) * mm});
            skLineSegment(sketch, "E1024", {"start": v(68.32, -29) * mm, "end": v(68.24, -28.77) * mm});
            skLineSegment(sketch, "E1025", {"start": v(68.24, -28.77) * mm, "end": v(68.1, -28.51) * mm});
            skLineSegment(sketch, "E1026", {"start": v(68.1, -28.51) * mm, "end": v(67.65, -28.1) * mm});
            skLineSegment(sketch, "E1027", {"start": v(67.65, -28.1) * mm, "end": v(65.18, -26.8) * mm});
            skLineSegment(sketch, "E1028", {"start": v(65.18, -26.8) * mm, "end": v(62.85, -25.3) * mm});
            skLineSegment(sketch, "E1029", {"start": v(62.85, -25.3) * mm, "end": v(62.26, -25.1) * mm});
            skLineSegment(sketch, "E1030", {"start": v(62.26, -25.1) * mm, "end": v(61.97, -25.12) * mm});
            skLineSegment(sketch, "E1031", {"start": v(61.97, -25.12) * mm, "end": v(61.73, -25.17) * mm});
            skLineSegment(sketch, "E1032", {"start": v(61.73, -25.17) * mm, "end": v(61.52, -25.23) * mm});
            skLineSegment(sketch, "E1033", {"start": v(61.52, -25.23) * mm, "end": v(61.32, -25.32) * mm});
            skLineSegment(sketch, "E1034", {"start": v(61.32, -25.32) * mm, "end": v(61.14, -25.4) * mm});
            skLineSegment(sketch, "E1035", {"start": v(61.14, -25.4) * mm, "end": v(60.8, -25.61) * mm});
            skLineSegment(sketch, "E1036", {"start": v(60.8, -25.61) * mm, "end": v(60.5, -25.84) * mm});
            skLineSegment(sketch, "E1037", {"start": v(60.5, -25.84) * mm, "end": v(60.22, -26.1) * mm});
            skLineSegment(sketch, "E1038", {"start": v(60.22, -26.1) * mm, "end": v(59.72, -26.63) * mm});
            skLineSegment(sketch, "E1039", {"start": v(59.72, -26.63) * mm, "end": v(59.24, -27.18) * mm});
            skLineSegment(sketch, "E1040", {"start": v(59.24, -27.18) * mm, "end": v(58.66, -27.66) * mm});
            skLineSegment(sketch, "E1041", {"start": v(58.66, -27.66) * mm, "end": v(58.03, -28.1) * mm});
            skLineSegment(sketch, "E1042", {"start": v(58.03, -28.1) * mm, "end": v(57.36, -28.5) * mm});
            skLineSegment(sketch, "E1043", {"start": v(57.36, -28.5) * mm, "end": v(56.65, -28.86) * mm});
            skLineSegment(sketch, "E1044", {"start": v(56.65, -28.86) * mm, "end": v(55.91, -29.2) * mm});
            skLineSegment(sketch, "E1045", {"start": v(55.91, -29.2) * mm, "end": v(55.14, -29.5) * mm});
            skLineSegment(sketch, "E1046", {"start": v(55.14, -29.5) * mm, "end": v(54.34, -29.78) * mm});
            skLineSegment(sketch, "E1047", {"start": v(54.34, -29.78) * mm, "end": v(53.52, -30.03) * mm});
            skLineSegment(sketch, "E1048", {"start": v(53.52, -30.03) * mm, "end": v(52.67, -30.25) * mm});
            skLineSegment(sketch, "E1049", {"start": v(52.67, -30.25) * mm, "end": v(51.8, -30.43) * mm});
            skLineSegment(sketch, "E1050", {"start": v(51.8, -30.43) * mm, "end": v(47.3, -25.4) * mm});
            skLineSegment(sketch, "E1051", {"start": v(47.3, -25.4) * mm, "end": v(47.58, -24.55) * mm});
            skLineSegment(sketch, "E1052", {"start": v(47.58, -24.55) * mm, "end": v(47.9, -23.73) * mm});
            skLineSegment(sketch, "E1053", {"start": v(47.9, -23.73) * mm, "end": v(48.23, -22.94) * mm});
            skLineSegment(sketch, "E1054", {"start": v(48.23, -22.94) * mm, "end": v(48.6, -22.18) * mm});
            skLineSegment(sketch, "E1055", {"start": v(48.6, -22.18) * mm, "end": v(49, -21.45) * mm});
            skLineSegment(sketch, "E1056", {"start": v(49, -21.45) * mm, "end": v(49.4, -20.75) * mm});
            skLineSegment(sketch, "E1057", {"start": v(49.4, -20.75) * mm, "end": v(49.85, -20.09) * mm});
            skLineSegment(sketch, "E1058", {"start": v(49.85, -20.09) * mm, "end": v(50.33, -19.47) * mm});
            skLineSegment(sketch, "E1059", {"start": v(50.33, -19.47) * mm, "end": v(50.83, -18.9) * mm});
            skLineSegment(sketch, "E1060", {"start": v(50.83, -18.9) * mm, "end": v(51.37, -18.37) * mm});
            skLineSegment(sketch, "E1061", {"start": v(51.37, -18.37) * mm, "end": v(51.98, -17.95) * mm});
            skLineSegment(sketch, "E1062", {"start": v(51.98, -17.95) * mm, "end": v(52.57, -17.51) * mm});
            skLineSegment(sketch, "E1063", {"start": v(52.57, -17.51) * mm, "end": v(52.84, -17.26) * mm});
            skLineSegment(sketch, "E1064", {"start": v(52.84, -17.26) * mm, "end": v(53.1, -16.99) * mm});
            skLineSegment(sketch, "E1065", {"start": v(53.1, -16.99) * mm, "end": v(53.35, -16.68) * mm});
            skLineSegment(sketch, "E1066", {"start": v(53.35, -16.68) * mm, "end": v(53.46, -16.51) * mm});
            skLineSegment(sketch, "E1067", {"start": v(53.46, -16.51) * mm, "end": v(53.56, -16.33) * mm});
            skLineSegment(sketch, "E1068", {"start": v(53.56, -16.33) * mm, "end": v(53.65, -16.12) * mm});
            skLineSegment(sketch, "E1069", {"start": v(53.65, -16.12) * mm, "end": v(53.73, -15.89) * mm});
            skLineSegment(sketch, "E1070", {"start": v(53.73, -15.89) * mm, "end": v(53.77, -15.6) * mm});
            skLineSegment(sketch, "E1071", {"start": v(53.77, -15.6) * mm, "end": v(53.64, -15) * mm});
            skLineSegment(sketch, "E1072", {"start": v(53.64, -15) * mm, "end": v(52.41, -12.5) * mm});
            skLineSegment(sketch, "E1073", {"start": v(52.41, -12.5) * mm, "end": v(51.4, -9.91) * mm});
            skLineSegment(sketch, "E1074", {"start": v(83.99, 0) * mm, "end": v(83.88, 0.82) * mm});
            skLineSegment(sketch, "E1075", {"start": v(83.88, 0.82) * mm, "end": v(83.56, 1.59) * mm});
            skLineSegment(sketch, "E1076", {"start": v(83.56, 1.59) * mm, "end": v(83.06, 2.25) * mm});
            skLineSegment(sketch, "E1077", {"start": v(83.06, 2.25) * mm, "end": v(82.4, 2.75) * mm});
            skLineSegment(sketch, "E1078", {"start": v(82.4, 2.75) * mm, "end": v(81.64, 3.07) * mm});
            skLineSegment(sketch, "E1079", {"start": v(81.64, 3.07) * mm, "end": v(80.81, 3.18) * mm});
            skLineSegment(sketch, "E1080", {"start": v(80.81, 3.18) * mm, "end": v(80, 3.07) * mm});
            skLineSegment(sketch, "E1081", {"start": v(80, 3.07) * mm, "end": v(79.23, 2.75) * mm});
            skLineSegment(sketch, "E1082", {"start": v(79.23, 2.75) * mm, "end": v(78.57, 2.25) * mm});
            skLineSegment(sketch, "E1083", {"start": v(78.57, 2.25) * mm, "end": v(78.06, 1.59) * mm});
            skLineSegment(sketch, "E1084", {"start": v(78.06, 1.59) * mm, "end": v(77.75, 0.82) * mm});
            skLineSegment(sketch, "E1085", {"start": v(77.75, 0.82) * mm, "end": v(77.64, 0) * mm});
            skLineSegment(sketch, "E1086", {"start": v(77.64, 0) * mm, "end": v(77.75, -0.82) * mm});
            skLineSegment(sketch, "E1087", {"start": v(77.75, -0.82) * mm, "end": v(78.06, -1.59) * mm});
            skLineSegment(sketch, "E1088", {"start": v(78.06, -1.59) * mm, "end": v(78.57, -2.25) * mm});
            skLineSegment(sketch, "E1089", {"start": v(78.57, -2.25) * mm, "end": v(79.23, -2.75) * mm});
            skLineSegment(sketch, "E1090", {"start": v(79.23, -2.75) * mm, "end": v(80, -3.07) * mm});
            skLineSegment(sketch, "E1091", {"start": v(80, -3.07) * mm, "end": v(80.81, -3.18) * mm});
            skLineSegment(sketch, "E1092", {"start": v(80.81, -3.18) * mm, "end": v(81.64, -3.07) * mm});
            skLineSegment(sketch, "E1093", {"start": v(81.64, -3.07) * mm, "end": v(82.4, -2.75) * mm});
            skLineSegment(sketch, "E1094", {"start": v(82.4, -2.75) * mm, "end": v(83.06, -2.25) * mm});
            skLineSegment(sketch, "E1095", {"start": v(83.06, -2.25) * mm, "end": v(83.56, -1.59) * mm});
            skLineSegment(sketch, "E1096", {"start": v(83.56, -1.59) * mm, "end": v(83.88, -0.82) * mm});
            skLineSegment(sketch, "E1097", {"start": v(83.88, -0.82) * mm, "end": v(83.99, 0) * mm});
            skSolve(sketch);
        }
        {
            var Q0;
            Q0=makeQuery(id+"F0.imprint","IMPRINT",FACE,{"disambiguationData":[TD([[makeQuery(id+"F0.imprint","IMPRINT",EDGE,{"derivedFrom":sQuery(id+"F0.wireOp",EDGE,"E0")}),-1.0]])]});
            var Q1;
            Q1=makeQuery(id+"F0.imprint","IMPRINT",FACE,{"disambiguationData":[TD([[makeQuery(id+"F0.imprint","IMPRINT",EDGE,{"derivedFrom":sQuery(id+"F0.wireOp",EDGE,"E624")}),-1.0]])]});
            extrude(context, id + "F1", {"entities" : qUnion([Q0, Q1]), "depth" : 19.05 * mm});
        }
    });
